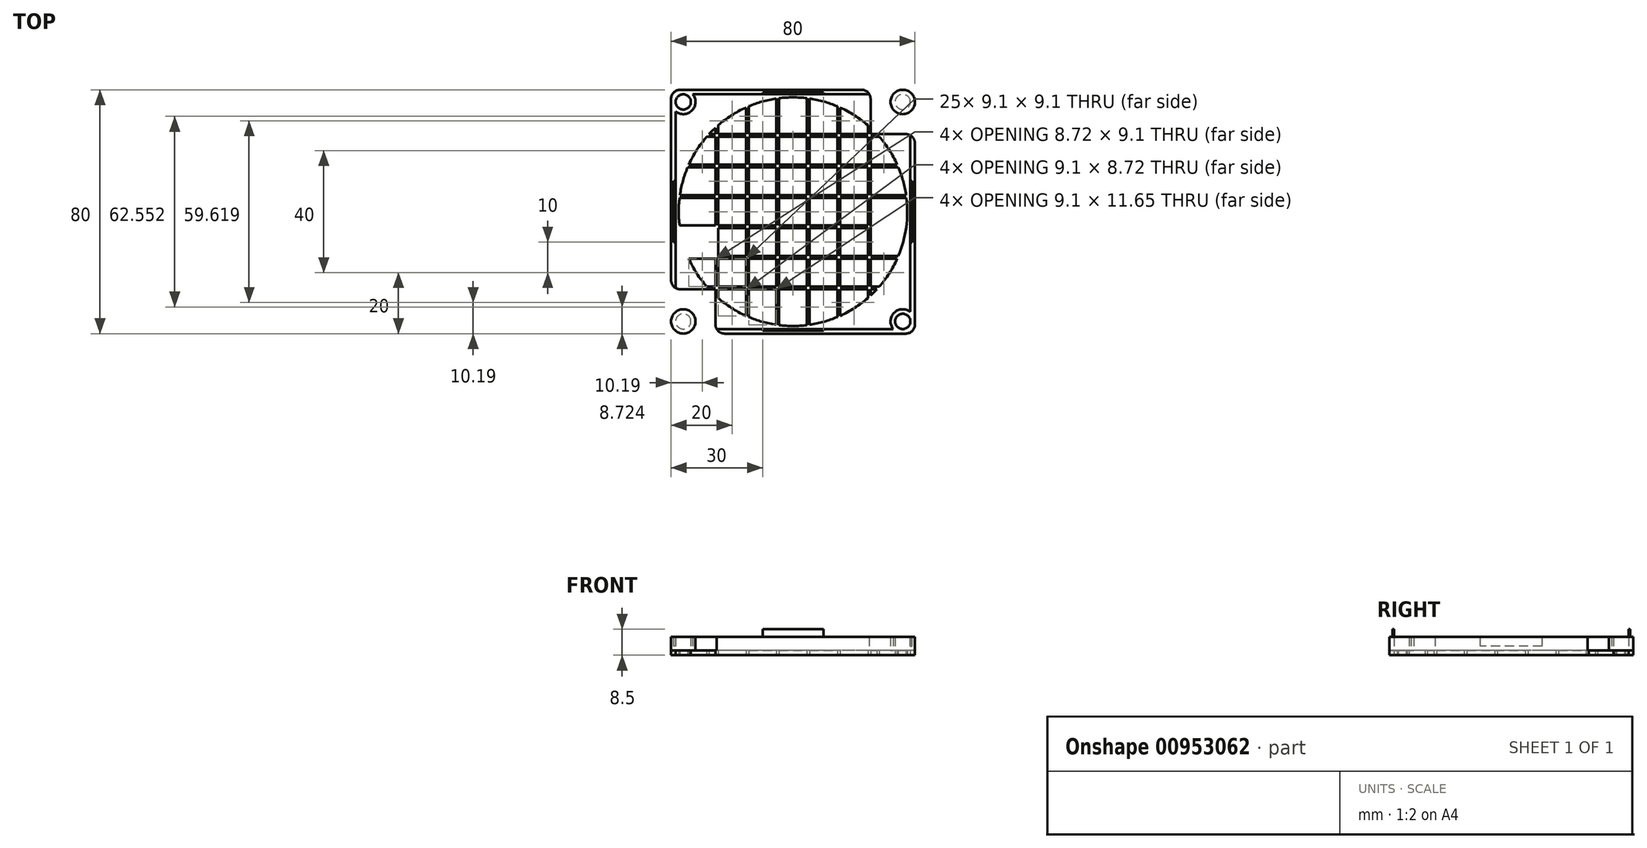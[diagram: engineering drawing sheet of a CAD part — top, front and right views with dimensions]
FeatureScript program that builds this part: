
annotation { "Feature Type Name" : "Feature", "Feature Type Description" : "" }
export const myFeature = defineFeature(function(context is Context, id is Id, definition is map)
    precondition{}
    {
        {
            var Q0;
            Q0=qCreatedBy(makeId("Top.planeOp"),FACE);
            var sketch = newSketch(context, id + "F0", { "sketchPlane" : qUnion([Q0])});
            skLineSegment(sketch, "E0.bottom", {"start": v(40, 40) * mm, "end": v(-40, 40) * mm});
            skLineSegment(sketch, "E0.top", {"start": v(40, -40) * mm, "end": v(-40, -40) * mm});
            skLineSegment(sketch, "E0.left", {"start": v(40, 40) * mm, "end": v(40, -40) * mm});
            skLineSegment(sketch, "E0.right", {"start": v(-40, 40) * mm, "end": v(-40, -40) * mm});
            skPoint(sketch, "E0.middle", {"position": v(0, 0) * mm});
            skCircle(sketch, "E1", {"center": v(-36, 36) * mm, "radius": 2.5 * mm});
            skCircle(sketch, "E2.MirrorC", {"center": v(36, 36) * mm, "radius": 2.5 * mm});
            skCircle(sketch, "E3.MirrorC", {"center": v(-36, -36) * mm, "radius": 2.5 * mm});
            skCircle(sketch, "E4.MirrorC", {"center": v(36, -36) * mm, "radius": 2.5 * mm});
            skCircle(sketch, "E5", {"center": v(0, 0) * mm, "radius": 37.5 * mm});
            skLineSegment(sketch, "E6.bottom", {"start": v(48.46, 5.45) * mm, "end": v(-48.46, 5.45) * mm});
            skLineSegment(sketch, "E6.top", {"start": v(48.46, 4.55) * mm, "end": v(-48.46, 4.55) * mm});
            skLineSegment(sketch, "E6.left", {"start": v(48.46, 5.45) * mm, "end": v(48.46, 4.55) * mm});
            skLineSegment(sketch, "E6.right", {"start": v(-48.46, 5.45) * mm, "end": v(-48.46, 4.55) * mm});
            skPoint(sketch, "E6.middle", {"position": v(0, 5) * mm});
            skLineSegment(sketch, "E7.bottom", {"start": v(55.87, 14.55) * mm, "end": v(-55.87, 14.55) * mm});
            skLineSegment(sketch, "E7.top", {"start": v(55.87, 15.45) * mm, "end": v(-55.87, 15.45) * mm});
            skLineSegment(sketch, "E7.left", {"start": v(55.87, 14.55) * mm, "end": v(55.87, 15.45) * mm});
            skLineSegment(sketch, "E7.right", {"start": v(-55.87, 14.55) * mm, "end": v(-55.87, 15.45) * mm});
            skPoint(sketch, "E7.middle", {"position": v(0, 15) * mm});
            skLineSegment(sketch, "E8.bottom", {"start": v(61.16, 24.55) * mm, "end": v(-61.16, 24.55) * mm});
            skLineSegment(sketch, "E8.top", {"start": v(61.16, 25.45) * mm, "end": v(-61.16, 25.45) * mm});
            skLineSegment(sketch, "E8.left", {"start": v(61.16, 24.55) * mm, "end": v(61.16, 25.45) * mm});
            skLineSegment(sketch, "E8.right", {"start": v(-61.16, 24.55) * mm, "end": v(-61.16, 25.45) * mm});
            skPoint(sketch, "E8.middle", {"position": v(0, 25) * mm});
            skLineSegment(sketch, "E9", {"start": v(0, 0) * mm, "end": v(40, 40) * mm});
            skLineSegment(sketch, "E10.MirrorCS", {"start": v(48.46, -4.55) * mm, "end": v(-48.46, -4.55) * mm});
            skLineSegment(sketch, "E11.MirrorCS", {"start": v(48.46, -5.45) * mm, "end": v(-48.46, -5.45) * mm});
            skLineSegment(sketch, "E12.MirrorCS", {"start": v(55.87, -14.55) * mm, "end": v(-55.87, -14.55) * mm});
            skLineSegment(sketch, "E13.MirrorCS", {"start": v(55.87, -15.45) * mm, "end": v(-55.87, -15.45) * mm});
            skLineSegment(sketch, "E14.MirrorCS", {"start": v(61.16, -24.55) * mm, "end": v(-61.16, -24.55) * mm});
            skLineSegment(sketch, "E15.MirrorCS", {"start": v(61.16, -25.45) * mm, "end": v(-61.16, -25.45) * mm});
            skLineSegment(sketch, "E16.MirrorCS", {"start": v(25.45, 61.16) * mm, "end": v(25.45, -61.16) * mm});
            skLineSegment(sketch, "E17.MirrorCS", {"start": v(24.55, 61.16) * mm, "end": v(24.55, -61.16) * mm});
            skLineSegment(sketch, "E18.MirrorCS", {"start": v(15.45, 55.87) * mm, "end": v(15.45, -55.87) * mm});
            skLineSegment(sketch, "E19.MirrorCS", {"start": v(14.55, 55.87) * mm, "end": v(14.55, -55.87) * mm});
            skLineSegment(sketch, "E20.MirrorCS", {"start": v(5.45, 48.46) * mm, "end": v(5.45, -48.46) * mm});
            skLineSegment(sketch, "E21.MirrorCS", {"start": v(4.55, 48.46) * mm, "end": v(4.55, -48.46) * mm});
            skLineSegment(sketch, "E22.MirrorCS", {"start": v(-4.55, 48.46) * mm, "end": v(-4.55, -48.46) * mm});
            skLineSegment(sketch, "E23.MirrorCS", {"start": v(-5.45, 48.46) * mm, "end": v(-5.45, -48.46) * mm});
            skLineSegment(sketch, "E24.MirrorCS", {"start": v(-14.55, 55.87) * mm, "end": v(-14.55, -55.87) * mm});
            skLineSegment(sketch, "E25.MirrorCS", {"start": v(-15.45, 55.87) * mm, "end": v(-15.45, -55.87) * mm});
            skLineSegment(sketch, "E26.MirrorCS", {"start": v(-24.55, 61.16) * mm, "end": v(-24.55, -61.16) * mm});
            skLineSegment(sketch, "E27.MirrorCS", {"start": v(-25.45, 61.16) * mm, "end": v(-25.45, -61.16) * mm});
            skSolve(sketch);
        }
        {
            var Q0;
            Q0=makeQuery(id+"F0.imprint","IMPRINT",FACE,{"disambiguationData":[TD([[makeQuery(id+"F0.imprint","IMPRINT",EDGE,{"derivedFrom":sQuery(id+"F0.wireOp",EDGE,"E0.bottom")}),1.0]])]});
            var Q1;
            Q1=makeQuery(id+"F0.imprint","IMPRINT",FACE,{"disambiguationData":[TD([[makeQuery(id+"F0.imprint","IMPRINT",EDGE,{"derivedFrom":sQuery(id+"F0.wireOp",EDGE,"E1")}),-1.0]])]});
            var Q2;
            {var subQ0=sQuery(id+"F0.wireOp",EDGE,"E8.bottom");var subQ1=sQuery(id+"F0.wireOp",EDGE,"E0.right");var subQ2=makeQuery(id+"F0.imprint","INTERSECT",VERTEX,{"derivedFrom":[subQ1,subQ0]});Q2=makeQuery(id+"F0.imprint","IMPRINT",FACE,{"disambiguationData":[TD([[makeQuery(id+"F0.imprint","IMPRINT",EDGE,{"disambiguationData":[TD([[subQ2,-1.0]])],"derivedFrom":subQ1}),1.0]])]});}
            var Q3;
            {var subQ0=sQuery(id+"F0.wireOp",EDGE,"E8.top");var subQ1=sQuery(id+"F0.wireOp",EDGE,"E0.right");var subQ2=makeQuery(id+"F0.imprint","INTERSECT",VERTEX,{"derivedFrom":[subQ1,subQ0]});Q3=makeQuery(id+"F0.imprint","IMPRINT",FACE,{"disambiguationData":[TD([[makeQuery(id+"F0.imprint","IMPRINT",EDGE,{"disambiguationData":[TD([[subQ2,-1.0]])],"derivedFrom":subQ1}),1.0]])]});}
            var Q4;
            {var subQ0=sQuery(id+"F0.wireOp",EDGE,"E26.MirrorCS");var subQ1=sQuery(id+"F0.wireOp",EDGE,"E8.bottom");var subQ2=makeQuery(id+"F0.imprint","INTERSECT",VERTEX,{"derivedFrom":[subQ1,subQ0]});Q4=makeQuery(id+"F0.imprint","IMPRINT",FACE,{"disambiguationData":[TD([[makeQuery(id+"F0.imprint","IMPRINT",EDGE,{"disambiguationData":[TD([[subQ2,-1.0]])],"derivedFrom":subQ1}),-1.0]])]});}
            var Q5;
            {var subQ0=sQuery(id+"F0.wireOp",EDGE,"E26.MirrorCS");var subQ1=sQuery(id+"F0.wireOp",EDGE,"E5");var subQ2=makeQuery(id+"F0.imprint","INTERSECT",VERTEX,{"disambiguationData":[OD(0.0)],"derivedFrom":[subQ1,subQ0]});Q5=makeQuery(id+"F0.imprint","IMPRINT",FACE,{"disambiguationData":[TD([[makeQuery(id+"F0.imprint","IMPRINT",EDGE,{"disambiguationData":[TD([[subQ2,-1.0]])],"derivedFrom":subQ1}),1.0]])]});}
            var Q6;
            {var subQ0=sQuery(id+"F0.wireOp",EDGE,"E8.top");var subQ1=sQuery(id+"F0.wireOp",EDGE,"E5");var subQ2=makeQuery(id+"F0.imprint","INTERSECT",VERTEX,{"disambiguationData":[OD(1.0)],"derivedFrom":[subQ1,subQ0]});Q6=makeQuery(id+"F0.imprint","IMPRINT",FACE,{"disambiguationData":[TD([[makeQuery(id+"F0.imprint","IMPRINT",EDGE,{"disambiguationData":[TD([[subQ2,-1.0]])],"derivedFrom":subQ1}),1.0]])]});}
            var Q7;
            {var subQ0=sQuery(id+"F0.wireOp",EDGE,"E9");var subQ5=sQuery(id+"F0.wireOp",EDGE,"E2.MirrorC");var subQ6=makeQuery(id+"F0.imprint","INTERSECT",VERTEX,{"disambiguationData":[OD(0.0)],"derivedFrom":[subQ5,subQ0]});Q7=makeQuery(id+"F0.imprint","IMPRINT",FACE,{"disambiguationData":[TD([[makeQuery(id+"F0.imprint","IMPRINT",EDGE,{"disambiguationData":[TD([[subQ6,-1.0]])],"derivedFrom":subQ5}),1.0]])]});}
            var Q8;
            {var subQ0=sQuery(id+"F0.wireOp",EDGE,"E13.MirrorCS");var subQ1=sQuery(id+"F0.wireOp",EDGE,"E0.left");var subQ2=makeQuery(id+"F0.imprint","INTERSECT",VERTEX,{"derivedFrom":[subQ1,subQ0]});Q8=makeQuery(id+"F0.imprint","IMPRINT",FACE,{"disambiguationData":[TD([[makeQuery(id+"F0.imprint","IMPRINT",EDGE,{"disambiguationData":[TD([[subQ2,-1.0]])],"derivedFrom":subQ1}),-1.0]])]});}
            var Q9;
            {var subQ0=sQuery(id+"F0.wireOp",EDGE,"E11.MirrorCS");var subQ1=sQuery(id+"F0.wireOp",EDGE,"E0.left");var subQ2=makeQuery(id+"F0.imprint","INTERSECT",VERTEX,{"derivedFrom":[subQ1,subQ0]});Q9=makeQuery(id+"F0.imprint","IMPRINT",FACE,{"disambiguationData":[TD([[makeQuery(id+"F0.imprint","IMPRINT",EDGE,{"disambiguationData":[TD([[subQ2,-1.0]])],"derivedFrom":subQ1}),-1.0]])]});}
            var Q10;
            {var subQ0=sQuery(id+"F0.wireOp",EDGE,"E7.bottom");var subQ1=sQuery(id+"F0.wireOp",EDGE,"E0.left");var subQ2=makeQuery(id+"F0.imprint","INTERSECT",VERTEX,{"derivedFrom":[subQ1,subQ0]});Q10=makeQuery(id+"F0.imprint","IMPRINT",FACE,{"disambiguationData":[TD([[makeQuery(id+"F0.imprint","IMPRINT",EDGE,{"disambiguationData":[TD([[subQ2,-1.0]])],"derivedFrom":subQ1}),-1.0]])]});}
            var Q11;
            {var subQ0=sQuery(id+"F0.wireOp",EDGE,"E8.bottom");var subQ1=sQuery(id+"F0.wireOp",EDGE,"E0.left");var subQ2=makeQuery(id+"F0.imprint","INTERSECT",VERTEX,{"derivedFrom":[subQ1,subQ0]});Q11=makeQuery(id+"F0.imprint","IMPRINT",FACE,{"disambiguationData":[TD([[makeQuery(id+"F0.imprint","IMPRINT",EDGE,{"disambiguationData":[TD([[subQ2,-1.0]])],"derivedFrom":subQ1}),-1.0]])]});}
            var Q12;
            {var subQ0=sQuery(id+"F0.wireOp",EDGE,"E8.top");var subQ1=sQuery(id+"F0.wireOp",EDGE,"E0.left");var subQ2=makeQuery(id+"F0.imprint","INTERSECT",VERTEX,{"derivedFrom":[subQ1,subQ0]});Q12=makeQuery(id+"F0.imprint","IMPRINT",FACE,{"disambiguationData":[TD([[makeQuery(id+"F0.imprint","IMPRINT",EDGE,{"disambiguationData":[TD([[subQ2,-1.0]])],"derivedFrom":subQ1}),-1.0]])]});}
            var Q13;
            {var subQ0=sQuery(id+"F0.wireOp",EDGE,"E25.MirrorCS");var subQ1=sQuery(id+"F0.wireOp",EDGE,"E0.top");var subQ2=makeQuery(id+"F0.imprint","INTERSECT",VERTEX,{"derivedFrom":[subQ1,subQ0]});Q13=makeQuery(id+"F0.imprint","IMPRINT",FACE,{"disambiguationData":[TD([[makeQuery(id+"F0.imprint","IMPRINT",EDGE,{"disambiguationData":[TD([[subQ2,-1.0]])],"derivedFrom":subQ1}),-1.0]])]});}
            var Q14;
            {var subQ0=sQuery(id+"F0.wireOp",EDGE,"E23.MirrorCS");var subQ1=sQuery(id+"F0.wireOp",EDGE,"E0.top");var subQ2=makeQuery(id+"F0.imprint","INTERSECT",VERTEX,{"derivedFrom":[subQ1,subQ0]});Q14=makeQuery(id+"F0.imprint","IMPRINT",FACE,{"disambiguationData":[TD([[makeQuery(id+"F0.imprint","IMPRINT",EDGE,{"disambiguationData":[TD([[subQ2,-1.0]])],"derivedFrom":subQ1}),-1.0]])]});}
            var Q15;
            {var subQ0=sQuery(id+"F0.wireOp",EDGE,"E11.MirrorCS");var subQ1=sQuery(id+"F0.wireOp",EDGE,"E0.right");var subQ2=makeQuery(id+"F0.imprint","INTERSECT",VERTEX,{"derivedFrom":[subQ1,subQ0]});Q15=makeQuery(id+"F0.imprint","IMPRINT",FACE,{"disambiguationData":[TD([[makeQuery(id+"F0.imprint","IMPRINT",EDGE,{"disambiguationData":[TD([[subQ2,-1.0]])],"derivedFrom":subQ1}),1.0]])]});}
            var Q16;
            {var subQ0=sQuery(id+"F0.wireOp",EDGE,"E7.bottom");var subQ1=sQuery(id+"F0.wireOp",EDGE,"E0.right");var subQ2=makeQuery(id+"F0.imprint","INTERSECT",VERTEX,{"derivedFrom":[subQ1,subQ0]});Q16=makeQuery(id+"F0.imprint","IMPRINT",FACE,{"disambiguationData":[TD([[makeQuery(id+"F0.imprint","IMPRINT",EDGE,{"disambiguationData":[TD([[subQ2,-1.0]])],"derivedFrom":subQ1}),1.0]])]});}
            var Q17;
            {var subQ0=sQuery(id+"F0.wireOp",EDGE,"E6.bottom");var subQ1=sQuery(id+"F0.wireOp",EDGE,"E5");var subQ2=makeQuery(id+"F0.imprint","INTERSECT",VERTEX,{"disambiguationData":[OD(1.0)],"derivedFrom":[subQ1,subQ0]});Q17=makeQuery(id+"F0.imprint","IMPRINT",FACE,{"disambiguationData":[TD([[makeQuery(id+"F0.imprint","IMPRINT",EDGE,{"disambiguationData":[TD([[subQ2,-1.0]])],"derivedFrom":subQ1}),1.0]])]});}
            var Q18;
            {var subQ0=sQuery(id+"F0.wireOp",EDGE,"E12.MirrorCS");var subQ1=sQuery(id+"F0.wireOp",EDGE,"E5");var subQ2=makeQuery(id+"F0.imprint","INTERSECT",VERTEX,{"disambiguationData":[OD(0.0)],"derivedFrom":[subQ1,subQ0]});Q18=makeQuery(id+"F0.imprint","IMPRINT",FACE,{"disambiguationData":[TD([[makeQuery(id+"F0.imprint","IMPRINT",EDGE,{"disambiguationData":[TD([[subQ2,-1.0]])],"derivedFrom":subQ1}),1.0]])]});}
            var Q19;
            {var subQ0=sQuery(id+"F0.wireOp",EDGE,"E10.MirrorCS");var subQ1=sQuery(id+"F0.wireOp",EDGE,"E5");var subQ2=makeQuery(id+"F0.imprint","INTERSECT",VERTEX,{"disambiguationData":[OD(0.0)],"derivedFrom":[subQ1,subQ0]});Q19=makeQuery(id+"F0.imprint","IMPRINT",FACE,{"disambiguationData":[TD([[makeQuery(id+"F0.imprint","IMPRINT",EDGE,{"disambiguationData":[TD([[subQ2,-1.0]])],"derivedFrom":subQ1}),1.0]])]});}
            var Q20;
            {var subQ0=sQuery(id+"F0.wireOp",EDGE,"E26.MirrorCS");var subQ1=sQuery(id+"F0.wireOp",EDGE,"E10.MirrorCS");var subQ2=makeQuery(id+"F0.imprint","INTERSECT",VERTEX,{"derivedFrom":[subQ1,subQ0]});Q20=makeQuery(id+"F0.imprint","IMPRINT",FACE,{"disambiguationData":[TD([[makeQuery(id+"F0.imprint","IMPRINT",EDGE,{"disambiguationData":[TD([[subQ2,-1.0]])],"derivedFrom":subQ1}),1.0]])]});}
            var Q21;
            {var subQ0=sQuery(id+"F0.wireOp",EDGE,"E26.MirrorCS");var subQ1=sQuery(id+"F0.wireOp",EDGE,"E6.top");var subQ2=makeQuery(id+"F0.imprint","INTERSECT",VERTEX,{"derivedFrom":[subQ1,subQ0]});Q21=makeQuery(id+"F0.imprint","IMPRINT",FACE,{"disambiguationData":[TD([[makeQuery(id+"F0.imprint","IMPRINT",EDGE,{"disambiguationData":[TD([[subQ2,-1.0]])],"derivedFrom":subQ1}),1.0]])]});}
            var Q22;
            {var subQ0=sQuery(id+"F0.wireOp",EDGE,"E26.MirrorCS");var subQ1=sQuery(id+"F0.wireOp",EDGE,"E6.bottom");var subQ2=makeQuery(id+"F0.imprint","INTERSECT",VERTEX,{"derivedFrom":[subQ1,subQ0]});Q22=makeQuery(id+"F0.imprint","IMPRINT",FACE,{"disambiguationData":[TD([[makeQuery(id+"F0.imprint","IMPRINT",EDGE,{"disambiguationData":[TD([[subQ2,-1.0]])],"derivedFrom":subQ1}),1.0]])]});}
            var Q23;
            {var subQ0=sQuery(id+"F0.wireOp",EDGE,"E26.MirrorCS");var subQ1=sQuery(id+"F0.wireOp",EDGE,"E6.bottom");var subQ2=makeQuery(id+"F0.imprint","INTERSECT",VERTEX,{"derivedFrom":[subQ1,subQ0]});Q23=makeQuery(id+"F0.imprint","IMPRINT",FACE,{"disambiguationData":[TD([[makeQuery(id+"F0.imprint","IMPRINT",EDGE,{"disambiguationData":[TD([[subQ2,-1.0]])],"derivedFrom":subQ1}),-1.0]])]});}
            var Q24;
            {var subQ0=sQuery(id+"F0.wireOp",EDGE,"E26.MirrorCS");var subQ1=sQuery(id+"F0.wireOp",EDGE,"E7.bottom");var subQ2=makeQuery(id+"F0.imprint","INTERSECT",VERTEX,{"derivedFrom":[subQ1,subQ0]});Q24=makeQuery(id+"F0.imprint","IMPRINT",FACE,{"disambiguationData":[TD([[makeQuery(id+"F0.imprint","IMPRINT",EDGE,{"disambiguationData":[TD([[subQ2,-1.0]])],"derivedFrom":subQ1}),-1.0]])]});}
            var Q25;
            {var subQ0=sQuery(id+"F0.wireOp",EDGE,"E7.top");var subQ1=sQuery(id+"F0.wireOp",EDGE,"E5");var subQ2=makeQuery(id+"F0.imprint","INTERSECT",VERTEX,{"disambiguationData":[OD(1.0)],"derivedFrom":[subQ1,subQ0]});Q25=makeQuery(id+"F0.imprint","IMPRINT",FACE,{"disambiguationData":[TD([[makeQuery(id+"F0.imprint","IMPRINT",EDGE,{"disambiguationData":[TD([[subQ2,-1.0]])],"derivedFrom":subQ1}),1.0]])]});}
            var Q26;
            {var subQ0=sQuery(id+"F0.wireOp",EDGE,"E26.MirrorCS");var subQ1=sQuery(id+"F0.wireOp",EDGE,"E7.top");var subQ2=makeQuery(id+"F0.imprint","INTERSECT",VERTEX,{"derivedFrom":[subQ1,subQ0]});Q26=makeQuery(id+"F0.imprint","IMPRINT",FACE,{"disambiguationData":[TD([[makeQuery(id+"F0.imprint","IMPRINT",EDGE,{"disambiguationData":[TD([[subQ2,-1.0]])],"derivedFrom":subQ1}),-1.0]])]});}
            var Q27;
            {var subQ0=sQuery(id+"F0.wireOp",EDGE,"E7.top");var subQ1=sQuery(id+"F0.wireOp",EDGE,"E0.right");var subQ2=makeQuery(id+"F0.imprint","INTERSECT",VERTEX,{"derivedFrom":[subQ1,subQ0]});Q27=makeQuery(id+"F0.imprint","IMPRINT",FACE,{"disambiguationData":[TD([[makeQuery(id+"F0.imprint","IMPRINT",EDGE,{"disambiguationData":[TD([[subQ2,-1.0]])],"derivedFrom":subQ1}),1.0]])]});}
            var Q28;
            {var subQ0=sQuery(id+"F0.wireOp",EDGE,"E6.bottom");var subQ1=sQuery(id+"F0.wireOp",EDGE,"E0.right");var subQ2=makeQuery(id+"F0.imprint","INTERSECT",VERTEX,{"derivedFrom":[subQ1,subQ0]});Q28=makeQuery(id+"F0.imprint","IMPRINT",FACE,{"disambiguationData":[TD([[makeQuery(id+"F0.imprint","IMPRINT",EDGE,{"disambiguationData":[TD([[subQ2,-1.0]])],"derivedFrom":subQ1}),1.0]])]});}
            var Q29;
            {var subQ0=sQuery(id+"F0.wireOp",EDGE,"E10.MirrorCS");var subQ1=sQuery(id+"F0.wireOp",EDGE,"E0.right");var subQ2=makeQuery(id+"F0.imprint","INTERSECT",VERTEX,{"derivedFrom":[subQ1,subQ0]});Q29=makeQuery(id+"F0.imprint","IMPRINT",FACE,{"disambiguationData":[TD([[makeQuery(id+"F0.imprint","IMPRINT",EDGE,{"disambiguationData":[TD([[subQ2,1.0]])],"derivedFrom":subQ1}),1.0]])]});}
            var Q30;
            {var subQ0=sQuery(id+"F0.wireOp",EDGE,"E10.MirrorCS");var subQ1=sQuery(id+"F0.wireOp",EDGE,"E0.right");var subQ2=makeQuery(id+"F0.imprint","INTERSECT",VERTEX,{"derivedFrom":[subQ1,subQ0]});Q30=makeQuery(id+"F0.imprint","IMPRINT",FACE,{"disambiguationData":[TD([[makeQuery(id+"F0.imprint","IMPRINT",EDGE,{"disambiguationData":[TD([[subQ2,-1.0]])],"derivedFrom":subQ1}),1.0]])]});}
            var Q31;
            {var subQ0=sQuery(id+"F0.wireOp",EDGE,"E12.MirrorCS");var subQ1=sQuery(id+"F0.wireOp",EDGE,"E0.right");var subQ2=makeQuery(id+"F0.imprint","INTERSECT",VERTEX,{"derivedFrom":[subQ1,subQ0]});Q31=makeQuery(id+"F0.imprint","IMPRINT",FACE,{"disambiguationData":[TD([[makeQuery(id+"F0.imprint","IMPRINT",EDGE,{"disambiguationData":[TD([[subQ2,-1.0]])],"derivedFrom":subQ1}),1.0]])]});}
            var Q32;
            {var subQ0=sQuery(id+"F0.wireOp",EDGE,"E13.MirrorCS");var subQ1=sQuery(id+"F0.wireOp",EDGE,"E0.right");var subQ2=makeQuery(id+"F0.imprint","INTERSECT",VERTEX,{"derivedFrom":[subQ1,subQ0]});Q32=makeQuery(id+"F0.imprint","IMPRINT",FACE,{"disambiguationData":[TD([[makeQuery(id+"F0.imprint","IMPRINT",EDGE,{"disambiguationData":[TD([[subQ2,-1.0]])],"derivedFrom":subQ1}),1.0]])]});}
            var Q33;
            {var subQ0=sQuery(id+"F0.wireOp",EDGE,"E14.MirrorCS");var subQ1=sQuery(id+"F0.wireOp",EDGE,"E0.right");var subQ2=makeQuery(id+"F0.imprint","INTERSECT",VERTEX,{"derivedFrom":[subQ1,subQ0]});Q33=makeQuery(id+"F0.imprint","IMPRINT",FACE,{"disambiguationData":[TD([[makeQuery(id+"F0.imprint","IMPRINT",EDGE,{"disambiguationData":[TD([[subQ2,-1.0]])],"derivedFrom":subQ1}),1.0]])]});}
            var Q34;
            Q34=makeQuery(id+"F0.imprint","IMPRINT",FACE,{"disambiguationData":[TD([[makeQuery(id+"F0.imprint","IMPRINT",EDGE,{"derivedFrom":sQuery(id+"F0.wireOp",EDGE,"E3.MirrorC")}),1.0]])]});
            var Q35;
            {var subQ0=sQuery(id+"F0.wireOp",EDGE,"E26.MirrorCS");var subQ1=sQuery(id+"F0.wireOp",EDGE,"E0.top");var subQ2=makeQuery(id+"F0.imprint","INTERSECT",VERTEX,{"derivedFrom":[subQ1,subQ0]});Q35=makeQuery(id+"F0.imprint","IMPRINT",FACE,{"disambiguationData":[TD([[makeQuery(id+"F0.imprint","IMPRINT",EDGE,{"disambiguationData":[TD([[subQ2,-1.0]])],"derivedFrom":subQ1}),-1.0]])]});}
            var Q36;
            {var subQ0=sQuery(id+"F0.wireOp",EDGE,"E24.MirrorCS");var subQ1=sQuery(id+"F0.wireOp",EDGE,"E0.top");var subQ2=makeQuery(id+"F0.imprint","INTERSECT",VERTEX,{"derivedFrom":[subQ1,subQ0]});Q36=makeQuery(id+"F0.imprint","IMPRINT",FACE,{"disambiguationData":[TD([[makeQuery(id+"F0.imprint","IMPRINT",EDGE,{"disambiguationData":[TD([[subQ2,-1.0]])],"derivedFrom":subQ1}),-1.0]])]});}
            var Q37;
            {var subQ0=sQuery(id+"F0.wireOp",EDGE,"E25.MirrorCS");var subQ1=sQuery(id+"F0.wireOp",EDGE,"E5");var subQ2=makeQuery(id+"F0.imprint","INTERSECT",VERTEX,{"disambiguationData":[OD(1.0)],"derivedFrom":[subQ1,subQ0]});Q37=makeQuery(id+"F0.imprint","IMPRINT",FACE,{"disambiguationData":[TD([[makeQuery(id+"F0.imprint","IMPRINT",EDGE,{"disambiguationData":[TD([[subQ2,-1.0]])],"derivedFrom":subQ1}),1.0]])]});}
            var Q38;
            {var subQ0=sQuery(id+"F0.wireOp",EDGE,"E24.MirrorCS");var subQ1=sQuery(id+"F0.wireOp",EDGE,"E14.MirrorCS");var subQ2=makeQuery(id+"F0.imprint","INTERSECT",VERTEX,{"derivedFrom":[subQ1,subQ0]});Q38=makeQuery(id+"F0.imprint","IMPRINT",FACE,{"disambiguationData":[TD([[makeQuery(id+"F0.imprint","IMPRINT",EDGE,{"disambiguationData":[TD([[subQ2,-1.0]])],"derivedFrom":subQ1}),1.0]])]});}
            var Q39;
            {var subQ0=sQuery(id+"F0.wireOp",EDGE,"E25.MirrorCS");var subQ1=sQuery(id+"F0.wireOp",EDGE,"E14.MirrorCS");var subQ2=makeQuery(id+"F0.imprint","INTERSECT",VERTEX,{"derivedFrom":[subQ1,subQ0]});Q39=makeQuery(id+"F0.imprint","IMPRINT",FACE,{"disambiguationData":[TD([[makeQuery(id+"F0.imprint","IMPRINT",EDGE,{"disambiguationData":[TD([[subQ2,-1.0]])],"derivedFrom":subQ1}),1.0]])]});}
            var Q40;
            {var subQ0=sQuery(id+"F0.wireOp",EDGE,"E24.MirrorCS");var subQ1=sQuery(id+"F0.wireOp",EDGE,"E13.MirrorCS");var subQ2=makeQuery(id+"F0.imprint","INTERSECT",VERTEX,{"derivedFrom":[subQ1,subQ0]});Q40=makeQuery(id+"F0.imprint","IMPRINT",FACE,{"disambiguationData":[TD([[makeQuery(id+"F0.imprint","IMPRINT",EDGE,{"disambiguationData":[TD([[subQ2,-1.0]])],"derivedFrom":subQ1}),1.0]])]});}
            var Q41;
            {var subQ0=sQuery(id+"F0.wireOp",EDGE,"E23.MirrorCS");var subQ1=sQuery(id+"F0.wireOp",EDGE,"E14.MirrorCS");var subQ2=makeQuery(id+"F0.imprint","INTERSECT",VERTEX,{"derivedFrom":[subQ1,subQ0]});Q41=makeQuery(id+"F0.imprint","IMPRINT",FACE,{"disambiguationData":[TD([[makeQuery(id+"F0.imprint","IMPRINT",EDGE,{"disambiguationData":[TD([[subQ2,-1.0]])],"derivedFrom":subQ1}),1.0]])]});}
            var Q42;
            {var subQ0=sQuery(id+"F0.wireOp",EDGE,"E22.MirrorCS");var subQ1=sQuery(id+"F0.wireOp",EDGE,"E13.MirrorCS");var subQ2=makeQuery(id+"F0.imprint","INTERSECT",VERTEX,{"derivedFrom":[subQ1,subQ0]});Q42=makeQuery(id+"F0.imprint","IMPRINT",FACE,{"disambiguationData":[TD([[makeQuery(id+"F0.imprint","IMPRINT",EDGE,{"disambiguationData":[TD([[subQ2,-1.0]])],"derivedFrom":subQ1}),1.0]])]});}
            var Q43;
            {var subQ0=sQuery(id+"F0.wireOp",EDGE,"E22.MirrorCS");var subQ1=sQuery(id+"F0.wireOp",EDGE,"E12.MirrorCS");var subQ2=makeQuery(id+"F0.imprint","INTERSECT",VERTEX,{"derivedFrom":[subQ1,subQ0]});Q43=makeQuery(id+"F0.imprint","IMPRINT",FACE,{"disambiguationData":[TD([[makeQuery(id+"F0.imprint","IMPRINT",EDGE,{"disambiguationData":[TD([[subQ2,-1.0]])],"derivedFrom":subQ1}),1.0]])]});}
            var Q44;
            {var subQ0=sQuery(id+"F0.wireOp",EDGE,"E22.MirrorCS");var subQ1=sQuery(id+"F0.wireOp",EDGE,"E11.MirrorCS");var subQ2=makeQuery(id+"F0.imprint","INTERSECT",VERTEX,{"derivedFrom":[subQ1,subQ0]});Q44=makeQuery(id+"F0.imprint","IMPRINT",FACE,{"disambiguationData":[TD([[makeQuery(id+"F0.imprint","IMPRINT",EDGE,{"disambiguationData":[TD([[subQ2,-1.0]])],"derivedFrom":subQ1}),1.0]])]});}
            var Q45;
            {var subQ0=sQuery(id+"F0.wireOp",EDGE,"E21.MirrorCS");var subQ1=sQuery(id+"F0.wireOp",EDGE,"E12.MirrorCS");var subQ2=makeQuery(id+"F0.imprint","INTERSECT",VERTEX,{"derivedFrom":[subQ1,subQ0]});Q45=makeQuery(id+"F0.imprint","IMPRINT",FACE,{"disambiguationData":[TD([[makeQuery(id+"F0.imprint","IMPRINT",EDGE,{"disambiguationData":[TD([[subQ2,-1.0]])],"derivedFrom":subQ1}),1.0]])]});}
            var Q46;
            {var subQ0=sQuery(id+"F0.wireOp",EDGE,"E20.MirrorCS");var subQ1=sQuery(id+"F0.wireOp",EDGE,"E12.MirrorCS");var subQ2=makeQuery(id+"F0.imprint","INTERSECT",VERTEX,{"derivedFrom":[subQ1,subQ0]});Q46=makeQuery(id+"F0.imprint","IMPRINT",FACE,{"disambiguationData":[TD([[makeQuery(id+"F0.imprint","IMPRINT",EDGE,{"disambiguationData":[TD([[subQ2,-1.0]])],"derivedFrom":subQ1}),1.0]])]});}
            var Q47;
            {var subQ0=sQuery(id+"F0.wireOp",EDGE,"E20.MirrorCS");var subQ1=sQuery(id+"F0.wireOp",EDGE,"E13.MirrorCS");var subQ2=makeQuery(id+"F0.imprint","INTERSECT",VERTEX,{"derivedFrom":[subQ1,subQ0]});Q47=makeQuery(id+"F0.imprint","IMPRINT",FACE,{"disambiguationData":[TD([[makeQuery(id+"F0.imprint","IMPRINT",EDGE,{"disambiguationData":[TD([[subQ2,-1.0]])],"derivedFrom":subQ1}),1.0]])]});}
            var Q48;
            {var subQ0=sQuery(id+"F0.wireOp",EDGE,"E20.MirrorCS");var subQ1=sQuery(id+"F0.wireOp",EDGE,"E11.MirrorCS");var subQ2=makeQuery(id+"F0.imprint","INTERSECT",VERTEX,{"derivedFrom":[subQ1,subQ0]});Q48=makeQuery(id+"F0.imprint","IMPRINT",FACE,{"disambiguationData":[TD([[makeQuery(id+"F0.imprint","IMPRINT",EDGE,{"disambiguationData":[TD([[subQ2,-1.0]])],"derivedFrom":subQ1}),1.0]])]});}
            var Q49;
            {var subQ0=sQuery(id+"F0.wireOp",EDGE,"E19.MirrorCS");var subQ1=sQuery(id+"F0.wireOp",EDGE,"E12.MirrorCS");var subQ2=makeQuery(id+"F0.imprint","INTERSECT",VERTEX,{"derivedFrom":[subQ1,subQ0]});Q49=makeQuery(id+"F0.imprint","IMPRINT",FACE,{"disambiguationData":[TD([[makeQuery(id+"F0.imprint","IMPRINT",EDGE,{"disambiguationData":[TD([[subQ2,-1.0]])],"derivedFrom":subQ1}),1.0]])]});}
            var Q50;
            {var subQ0=sQuery(id+"F0.wireOp",EDGE,"E17.MirrorCS");var subQ1=sQuery(id+"F0.wireOp",EDGE,"E14.MirrorCS");var subQ2=makeQuery(id+"F0.imprint","INTERSECT",VERTEX,{"derivedFrom":[subQ1,subQ0]});Q50=makeQuery(id+"F0.imprint","IMPRINT",FACE,{"disambiguationData":[TD([[makeQuery(id+"F0.imprint","IMPRINT",EDGE,{"disambiguationData":[TD([[subQ2,-1.0]])],"derivedFrom":subQ1}),1.0]])]});}
            var Q51;
            {var subQ0=sQuery(id+"F0.wireOp",EDGE,"E18.MirrorCS");var subQ1=sQuery(id+"F0.wireOp",EDGE,"E14.MirrorCS");var subQ2=makeQuery(id+"F0.imprint","INTERSECT",VERTEX,{"derivedFrom":[subQ1,subQ0]});Q51=makeQuery(id+"F0.imprint","IMPRINT",FACE,{"disambiguationData":[TD([[makeQuery(id+"F0.imprint","IMPRINT",EDGE,{"disambiguationData":[TD([[subQ2,-1.0]])],"derivedFrom":subQ1}),1.0]])]});}
            var Q52;
            {var subQ0=sQuery(id+"F0.wireOp",EDGE,"E19.MirrorCS");var subQ1=sQuery(id+"F0.wireOp",EDGE,"E14.MirrorCS");var subQ2=makeQuery(id+"F0.imprint","INTERSECT",VERTEX,{"derivedFrom":[subQ1,subQ0]});Q52=makeQuery(id+"F0.imprint","IMPRINT",FACE,{"disambiguationData":[TD([[makeQuery(id+"F0.imprint","IMPRINT",EDGE,{"disambiguationData":[TD([[subQ2,-1.0]])],"derivedFrom":subQ1}),1.0]])]});}
            var Q53;
            {var subQ0=sQuery(id+"F0.wireOp",EDGE,"E19.MirrorCS");var subQ1=sQuery(id+"F0.wireOp",EDGE,"E5");var subQ2=makeQuery(id+"F0.imprint","INTERSECT",VERTEX,{"disambiguationData":[OD(1.0)],"derivedFrom":[subQ1,subQ0]});Q53=makeQuery(id+"F0.imprint","IMPRINT",FACE,{"disambiguationData":[TD([[makeQuery(id+"F0.imprint","IMPRINT",EDGE,{"disambiguationData":[TD([[subQ2,-1.0]])],"derivedFrom":subQ1}),1.0]])]});}
            var Q54;
            {var subQ0=sQuery(id+"F0.wireOp",EDGE,"E17.MirrorCS");var subQ1=sQuery(id+"F0.wireOp",EDGE,"E0.top");var subQ2=makeQuery(id+"F0.imprint","INTERSECT",VERTEX,{"derivedFrom":[subQ1,subQ0]});Q54=makeQuery(id+"F0.imprint","IMPRINT",FACE,{"disambiguationData":[TD([[makeQuery(id+"F0.imprint","IMPRINT",EDGE,{"disambiguationData":[TD([[subQ2,-1.0]])],"derivedFrom":subQ1}),-1.0]])]});}
            var Q55;
            {var subQ0=sQuery(id+"F0.wireOp",EDGE,"E18.MirrorCS");var subQ1=sQuery(id+"F0.wireOp",EDGE,"E0.top");var subQ2=makeQuery(id+"F0.imprint","INTERSECT",VERTEX,{"derivedFrom":[subQ1,subQ0]});Q55=makeQuery(id+"F0.imprint","IMPRINT",FACE,{"disambiguationData":[TD([[makeQuery(id+"F0.imprint","IMPRINT",EDGE,{"disambiguationData":[TD([[subQ2,-1.0]])],"derivedFrom":subQ1}),-1.0]])]});}
            var Q56;
            {var subQ3=sQuery(id+"F0.wireOp",EDGE,"E9");var subQ5=sQuery(id+"F0.wireOp",EDGE,"E2.MirrorC");var subQ6=makeQuery(id+"F0.imprint","INTERSECT",VERTEX,{"disambiguationData":[OD(0.0)],"derivedFrom":[subQ5,subQ3]});Q56=makeQuery(id+"F0.imprint","IMPRINT",FACE,{"disambiguationData":[TD([[makeQuery(id+"F0.imprint","IMPRINT",EDGE,{"disambiguationData":[TD([[subQ6,1.0]])],"derivedFrom":subQ5}),1.0]])]});}
            var Q57;
            {var subQ0=sQuery(id+"F0.wireOp",EDGE,"E7.top");var subQ1=sQuery(id+"F0.wireOp",EDGE,"E0.left");var subQ2=makeQuery(id+"F0.imprint","INTERSECT",VERTEX,{"derivedFrom":[subQ1,subQ0]});Q57=makeQuery(id+"F0.imprint","IMPRINT",FACE,{"disambiguationData":[TD([[makeQuery(id+"F0.imprint","IMPRINT",EDGE,{"disambiguationData":[TD([[subQ2,-1.0]])],"derivedFrom":subQ1}),-1.0]])]});}
            var Q58;
            {var subQ0=sQuery(id+"F0.wireOp",EDGE,"E6.bottom");var subQ1=sQuery(id+"F0.wireOp",EDGE,"E0.left");var subQ2=makeQuery(id+"F0.imprint","INTERSECT",VERTEX,{"derivedFrom":[subQ1,subQ0]});Q58=makeQuery(id+"F0.imprint","IMPRINT",FACE,{"disambiguationData":[TD([[makeQuery(id+"F0.imprint","IMPRINT",EDGE,{"disambiguationData":[TD([[subQ2,-1.0]])],"derivedFrom":subQ1}),-1.0]])]});}
            var Q59;
            {var subQ0=sQuery(id+"F0.wireOp",EDGE,"E10.MirrorCS");var subQ1=sQuery(id+"F0.wireOp",EDGE,"E0.left");var subQ2=makeQuery(id+"F0.imprint","INTERSECT",VERTEX,{"derivedFrom":[subQ1,subQ0]});Q59=makeQuery(id+"F0.imprint","IMPRINT",FACE,{"disambiguationData":[TD([[makeQuery(id+"F0.imprint","IMPRINT",EDGE,{"disambiguationData":[TD([[subQ2,1.0]])],"derivedFrom":subQ1}),-1.0]])]});}
            var Q60;
            {var subQ0=sQuery(id+"F0.wireOp",EDGE,"E10.MirrorCS");var subQ1=sQuery(id+"F0.wireOp",EDGE,"E0.left");var subQ2=makeQuery(id+"F0.imprint","INTERSECT",VERTEX,{"derivedFrom":[subQ1,subQ0]});Q60=makeQuery(id+"F0.imprint","IMPRINT",FACE,{"disambiguationData":[TD([[makeQuery(id+"F0.imprint","IMPRINT",EDGE,{"disambiguationData":[TD([[subQ2,-1.0]])],"derivedFrom":subQ1}),-1.0]])]});}
            var Q61;
            {var subQ0=sQuery(id+"F0.wireOp",EDGE,"E12.MirrorCS");var subQ1=sQuery(id+"F0.wireOp",EDGE,"E0.left");var subQ2=makeQuery(id+"F0.imprint","INTERSECT",VERTEX,{"derivedFrom":[subQ1,subQ0]});Q61=makeQuery(id+"F0.imprint","IMPRINT",FACE,{"disambiguationData":[TD([[makeQuery(id+"F0.imprint","IMPRINT",EDGE,{"disambiguationData":[TD([[subQ2,-1.0]])],"derivedFrom":subQ1}),-1.0]])]});}
            var Q62;
            {var subQ0=sQuery(id+"F0.wireOp",EDGE,"E14.MirrorCS");var subQ1=sQuery(id+"F0.wireOp",EDGE,"E0.left");var subQ2=makeQuery(id+"F0.imprint","INTERSECT",VERTEX,{"derivedFrom":[subQ1,subQ0]});Q62=makeQuery(id+"F0.imprint","IMPRINT",FACE,{"disambiguationData":[TD([[makeQuery(id+"F0.imprint","IMPRINT",EDGE,{"disambiguationData":[TD([[subQ2,-1.0]])],"derivedFrom":subQ1}),-1.0]])]});}
            var Q63;
            {var subQ0=sQuery(id+"F0.wireOp",EDGE,"E7.bottom");var subQ1=sQuery(id+"F0.wireOp",EDGE,"E5");var subQ2=makeQuery(id+"F0.imprint","INTERSECT",VERTEX,{"disambiguationData":[OD(0.0)],"derivedFrom":[subQ1,subQ0]});Q63=makeQuery(id+"F0.imprint","IMPRINT",FACE,{"disambiguationData":[TD([[makeQuery(id+"F0.imprint","IMPRINT",EDGE,{"disambiguationData":[TD([[subQ2,-1.0]])],"derivedFrom":subQ1}),1.0]])]});}
            var Q64;
            {var subQ0=sQuery(id+"F0.wireOp",EDGE,"E17.MirrorCS");var subQ1=sQuery(id+"F0.wireOp",EDGE,"E7.bottom");var subQ2=makeQuery(id+"F0.imprint","INTERSECT",VERTEX,{"derivedFrom":[subQ1,subQ0]});Q64=makeQuery(id+"F0.imprint","IMPRINT",FACE,{"disambiguationData":[TD([[makeQuery(id+"F0.imprint","IMPRINT",EDGE,{"disambiguationData":[TD([[subQ2,-1.0]])],"derivedFrom":subQ1}),-1.0]])]});}
            var Q65;
            {var subQ0=sQuery(id+"F0.wireOp",EDGE,"E16.MirrorCS");var subQ1=sQuery(id+"F0.wireOp",EDGE,"E7.bottom");var subQ2=makeQuery(id+"F0.imprint","INTERSECT",VERTEX,{"derivedFrom":[subQ1,subQ0]});Q65=makeQuery(id+"F0.imprint","IMPRINT",FACE,{"disambiguationData":[TD([[makeQuery(id+"F0.imprint","IMPRINT",EDGE,{"disambiguationData":[TD([[subQ2,-1.0]])],"derivedFrom":subQ1}),-1.0]])]});}
            var Q66;
            {var subQ0=sQuery(id+"F0.wireOp",EDGE,"E16.MirrorCS");var subQ1=sQuery(id+"F0.wireOp",EDGE,"E7.top");var subQ2=makeQuery(id+"F0.imprint","INTERSECT",VERTEX,{"derivedFrom":[subQ1,subQ0]});Q66=makeQuery(id+"F0.imprint","IMPRINT",FACE,{"disambiguationData":[TD([[makeQuery(id+"F0.imprint","IMPRINT",EDGE,{"disambiguationData":[TD([[subQ2,-1.0]])],"derivedFrom":subQ1}),-1.0]])]});}
            var Q67;
            {var subQ0=sQuery(id+"F0.wireOp",EDGE,"E16.MirrorCS");var subQ1=sQuery(id+"F0.wireOp",EDGE,"E6.bottom");var subQ2=makeQuery(id+"F0.imprint","INTERSECT",VERTEX,{"derivedFrom":[subQ1,subQ0]});Q67=makeQuery(id+"F0.imprint","IMPRINT",FACE,{"disambiguationData":[TD([[makeQuery(id+"F0.imprint","IMPRINT",EDGE,{"disambiguationData":[TD([[subQ2,-1.0]])],"derivedFrom":subQ1}),-1.0]])]});}
            var Q68;
            {var subQ0=sQuery(id+"F0.wireOp",EDGE,"E8.bottom");var subQ1=sQuery(id+"F0.wireOp",EDGE,"E5");var subQ2=makeQuery(id+"F0.imprint","INTERSECT",VERTEX,{"disambiguationData":[OD(0.0)],"derivedFrom":[subQ1,subQ0]});Q68=makeQuery(id+"F0.imprint","IMPRINT",FACE,{"disambiguationData":[TD([[makeQuery(id+"F0.imprint","IMPRINT",EDGE,{"disambiguationData":[TD([[subQ2,-1.0]])],"derivedFrom":subQ1}),1.0]])]});}
            var Q69;
            {var subQ0=sQuery(id+"F0.wireOp",EDGE,"E16.MirrorCS");var subQ1=sQuery(id+"F0.wireOp",EDGE,"E8.bottom");var subQ2=makeQuery(id+"F0.imprint","INTERSECT",VERTEX,{"derivedFrom":[subQ1,subQ0]});Q69=makeQuery(id+"F0.imprint","IMPRINT",FACE,{"disambiguationData":[TD([[makeQuery(id+"F0.imprint","IMPRINT",EDGE,{"disambiguationData":[TD([[subQ2,-1.0]])],"derivedFrom":subQ1}),-1.0]])]});}
            var Q70;
            {var subQ0=sQuery(id+"F0.wireOp",EDGE,"E17.MirrorCS");var subQ1=sQuery(id+"F0.wireOp",EDGE,"E8.top");var subQ2=makeQuery(id+"F0.imprint","INTERSECT",VERTEX,{"derivedFrom":[subQ1,subQ0]});Q70=makeQuery(id+"F0.imprint","IMPRINT",FACE,{"disambiguationData":[TD([[makeQuery(id+"F0.imprint","IMPRINT",EDGE,{"disambiguationData":[TD([[subQ2,1.0]])],"derivedFrom":subQ1}),1.0]])]});}
            var Q71;
            {var subQ0=sQuery(id+"F0.wireOp",EDGE,"E16.MirrorCS");var subQ1=sQuery(id+"F0.wireOp",EDGE,"E5");var subQ2=makeQuery(id+"F0.imprint","INTERSECT",VERTEX,{"disambiguationData":[OD(0.0)],"derivedFrom":[subQ1,subQ0]});Q71=makeQuery(id+"F0.imprint","IMPRINT",FACE,{"disambiguationData":[TD([[makeQuery(id+"F0.imprint","IMPRINT",EDGE,{"disambiguationData":[TD([[subQ2,-1.0]])],"derivedFrom":subQ1}),1.0]])]});}
            var Q72;
            {var subQ3=sQuery(id+"F0.wireOp",EDGE,"E17.MirrorCS");var subQ5=sQuery(id+"F0.wireOp",EDGE,"E8.top");var subQ6=makeQuery(id+"F0.imprint","INTERSECT",VERTEX,{"derivedFrom":[subQ5,subQ3]});Q72=makeQuery(id+"F0.imprint","IMPRINT",FACE,{"disambiguationData":[TD([[makeQuery(id+"F0.imprint","IMPRINT",EDGE,{"disambiguationData":[TD([[subQ6,-1.0]])],"derivedFrom":subQ5}),1.0]])]});}
            var Q73;
            {var subQ0=sQuery(id+"F0.wireOp",EDGE,"E18.MirrorCS");var subQ1=sQuery(id+"F0.wireOp",EDGE,"E8.bottom");var subQ2=makeQuery(id+"F0.imprint","INTERSECT",VERTEX,{"derivedFrom":[subQ1,subQ0]});Q73=makeQuery(id+"F0.imprint","IMPRINT",FACE,{"disambiguationData":[TD([[makeQuery(id+"F0.imprint","IMPRINT",EDGE,{"disambiguationData":[TD([[subQ2,-1.0]])],"derivedFrom":subQ1}),-1.0]])]});}
            var Q74;
            {var subQ0=sQuery(id+"F0.wireOp",EDGE,"E18.MirrorCS");var subQ1=sQuery(id+"F0.wireOp",EDGE,"E5");var subQ2=makeQuery(id+"F0.imprint","INTERSECT",VERTEX,{"disambiguationData":[OD(0.0)],"derivedFrom":[subQ1,subQ0]});Q74=makeQuery(id+"F0.imprint","IMPRINT",FACE,{"disambiguationData":[TD([[makeQuery(id+"F0.imprint","IMPRINT",EDGE,{"disambiguationData":[TD([[subQ2,-1.0]])],"derivedFrom":subQ1}),1.0]])]});}
            var Q75;
            {var subQ3=sQuery(id+"F0.wireOp",EDGE,"E18.MirrorCS");var subQ5=sQuery(id+"F0.wireOp",EDGE,"E8.bottom");var subQ6=makeQuery(id+"F0.imprint","INTERSECT",VERTEX,{"derivedFrom":[subQ5,subQ3]});Q75=makeQuery(id+"F0.imprint","IMPRINT",FACE,{"disambiguationData":[TD([[makeQuery(id+"F0.imprint","IMPRINT",EDGE,{"disambiguationData":[TD([[subQ6,-1.0]])],"derivedFrom":subQ5}),1.0]])]});}
            var Q76;
            {var subQ0=sQuery(id+"F0.wireOp",EDGE,"E20.MirrorCS");var subQ1=sQuery(id+"F0.wireOp",EDGE,"E7.top");var subQ2=makeQuery(id+"F0.imprint","INTERSECT",VERTEX,{"derivedFrom":[subQ1,subQ0]});Q76=makeQuery(id+"F0.imprint","IMPRINT",FACE,{"disambiguationData":[TD([[makeQuery(id+"F0.imprint","IMPRINT",EDGE,{"disambiguationData":[TD([[subQ2,-1.0]])],"derivedFrom":subQ1}),-1.0]])]});}
            var Q77;
            {var subQ0=sQuery(id+"F0.wireOp",EDGE,"E22.MirrorCS");var subQ1=sQuery(id+"F0.wireOp",EDGE,"E7.top");var subQ2=makeQuery(id+"F0.imprint","INTERSECT",VERTEX,{"derivedFrom":[subQ1,subQ0]});Q77=makeQuery(id+"F0.imprint","IMPRINT",FACE,{"disambiguationData":[TD([[makeQuery(id+"F0.imprint","IMPRINT",EDGE,{"disambiguationData":[TD([[subQ2,-1.0]])],"derivedFrom":subQ1}),-1.0]])]});}
            var Q78;
            {var subQ0=sQuery(id+"F0.wireOp",EDGE,"E24.MirrorCS");var subQ1=sQuery(id+"F0.wireOp",EDGE,"E5");var subQ2=makeQuery(id+"F0.imprint","INTERSECT",VERTEX,{"disambiguationData":[OD(0.0)],"derivedFrom":[subQ1,subQ0]});Q78=makeQuery(id+"F0.imprint","IMPRINT",FACE,{"disambiguationData":[TD([[makeQuery(id+"F0.imprint","IMPRINT",EDGE,{"disambiguationData":[TD([[subQ2,-1.0]])],"derivedFrom":subQ1}),1.0]])]});}
            var Q79;
            {var subQ0=sQuery(id+"F0.wireOp",EDGE,"E25.MirrorCS");var subQ1=sQuery(id+"F0.wireOp",EDGE,"E8.bottom");var subQ2=makeQuery(id+"F0.imprint","INTERSECT",VERTEX,{"derivedFrom":[subQ1,subQ0]});Q79=makeQuery(id+"F0.imprint","IMPRINT",FACE,{"disambiguationData":[TD([[makeQuery(id+"F0.imprint","IMPRINT",EDGE,{"disambiguationData":[TD([[subQ2,-1.0]])],"derivedFrom":subQ1}),-1.0]])]});}
            var Q80;
            {var subQ0=sQuery(id+"F0.wireOp",EDGE,"E25.MirrorCS");var subQ1=sQuery(id+"F0.wireOp",EDGE,"E7.bottom");var subQ2=makeQuery(id+"F0.imprint","INTERSECT",VERTEX,{"derivedFrom":[subQ1,subQ0]});Q80=makeQuery(id+"F0.imprint","IMPRINT",FACE,{"disambiguationData":[TD([[makeQuery(id+"F0.imprint","IMPRINT",EDGE,{"disambiguationData":[TD([[subQ2,-1.0]])],"derivedFrom":subQ1}),-1.0]])]});}
            var Q81;
            {var subQ0=sQuery(id+"F0.wireOp",EDGE,"E23.MirrorCS");var subQ1=sQuery(id+"F0.wireOp",EDGE,"E6.bottom");var subQ2=makeQuery(id+"F0.imprint","INTERSECT",VERTEX,{"derivedFrom":[subQ1,subQ0]});Q81=makeQuery(id+"F0.imprint","IMPRINT",FACE,{"disambiguationData":[TD([[makeQuery(id+"F0.imprint","IMPRINT",EDGE,{"disambiguationData":[TD([[subQ2,-1.0]])],"derivedFrom":subQ1}),1.0]])]});}
            var Q82;
            {var subQ0=sQuery(id+"F0.wireOp",EDGE,"E24.MirrorCS");var subQ1=sQuery(id+"F0.wireOp",EDGE,"E6.top");var subQ2=makeQuery(id+"F0.imprint","INTERSECT",VERTEX,{"derivedFrom":[subQ1,subQ0]});Q82=makeQuery(id+"F0.imprint","IMPRINT",FACE,{"disambiguationData":[TD([[makeQuery(id+"F0.imprint","IMPRINT",EDGE,{"disambiguationData":[TD([[subQ2,-1.0]])],"derivedFrom":subQ1}),1.0]])]});}
            var Q83;
            {var subQ0=sQuery(id+"F0.wireOp",EDGE,"E25.MirrorCS");var subQ1=sQuery(id+"F0.wireOp",EDGE,"E6.bottom");var subQ2=makeQuery(id+"F0.imprint","INTERSECT",VERTEX,{"derivedFrom":[subQ1,subQ0]});Q83=makeQuery(id+"F0.imprint","IMPRINT",FACE,{"disambiguationData":[TD([[makeQuery(id+"F0.imprint","IMPRINT",EDGE,{"disambiguationData":[TD([[subQ2,-1.0]])],"derivedFrom":subQ1}),1.0]])]});}
            var Q84;
            {var subQ0=sQuery(id+"F0.wireOp",EDGE,"E24.MirrorCS");var subQ1=sQuery(id+"F0.wireOp",EDGE,"E11.MirrorCS");var subQ2=makeQuery(id+"F0.imprint","INTERSECT",VERTEX,{"derivedFrom":[subQ1,subQ0]});Q84=makeQuery(id+"F0.imprint","IMPRINT",FACE,{"disambiguationData":[TD([[makeQuery(id+"F0.imprint","IMPRINT",EDGE,{"disambiguationData":[TD([[subQ2,-1.0]])],"derivedFrom":subQ1}),1.0]])]});}
            var Q85;
            {var subQ0=sQuery(id+"F0.wireOp",EDGE,"E23.MirrorCS");var subQ1=sQuery(id+"F0.wireOp",EDGE,"E12.MirrorCS");var subQ2=makeQuery(id+"F0.imprint","INTERSECT",VERTEX,{"derivedFrom":[subQ1,subQ0]});Q85=makeQuery(id+"F0.imprint","IMPRINT",FACE,{"disambiguationData":[TD([[makeQuery(id+"F0.imprint","IMPRINT",EDGE,{"disambiguationData":[TD([[subQ2,-1.0]])],"derivedFrom":subQ1}),1.0]])]});}
            var Q86;
            {var subQ0=sQuery(id+"F0.wireOp",EDGE,"E25.MirrorCS");var subQ1=sQuery(id+"F0.wireOp",EDGE,"E12.MirrorCS");var subQ2=makeQuery(id+"F0.imprint","INTERSECT",VERTEX,{"derivedFrom":[subQ1,subQ0]});Q86=makeQuery(id+"F0.imprint","IMPRINT",FACE,{"disambiguationData":[TD([[makeQuery(id+"F0.imprint","IMPRINT",EDGE,{"disambiguationData":[TD([[subQ2,-1.0]])],"derivedFrom":subQ1}),1.0]])]});}
            var Q87;
            {var subQ0=sQuery(id+"F0.wireOp",EDGE,"E21.MirrorCS");var subQ1=sQuery(id+"F0.wireOp",EDGE,"E6.bottom");var subQ2=makeQuery(id+"F0.imprint","INTERSECT",VERTEX,{"derivedFrom":[subQ1,subQ0]});Q87=makeQuery(id+"F0.imprint","IMPRINT",FACE,{"disambiguationData":[TD([[makeQuery(id+"F0.imprint","IMPRINT",EDGE,{"disambiguationData":[TD([[subQ2,-1.0]])],"derivedFrom":subQ1}),1.0]])]});}
            var Q88;
            {var subQ3=sQuery(id+"F0.wireOp",EDGE,"E20.MirrorCS");var subQ5=sQuery(id+"F0.wireOp",EDGE,"E7.bottom");var subQ6=makeQuery(id+"F0.imprint","INTERSECT",VERTEX,{"derivedFrom":[subQ5,subQ3]});Q88=makeQuery(id+"F0.imprint","IMPRINT",FACE,{"disambiguationData":[TD([[makeQuery(id+"F0.imprint","IMPRINT",EDGE,{"disambiguationData":[TD([[subQ6,-1.0]])],"derivedFrom":subQ5}),1.0]])]});}
            var Q89;
            {var subQ0=sQuery(id+"F0.wireOp",EDGE,"E21.MirrorCS");var subQ1=sQuery(id+"F0.wireOp",EDGE,"E6.bottom");var subQ2=makeQuery(id+"F0.imprint","INTERSECT",VERTEX,{"derivedFrom":[subQ1,subQ0]});Q89=makeQuery(id+"F0.imprint","IMPRINT",FACE,{"disambiguationData":[TD([[makeQuery(id+"F0.imprint","IMPRINT",EDGE,{"disambiguationData":[TD([[subQ2,1.0]])],"derivedFrom":subQ1}),1.0]])]});}
            var Q90;
            {var subQ0=sQuery(id+"F0.wireOp",EDGE,"E19.MirrorCS");var subQ5=sQuery(id+"F0.wireOp",EDGE,"E6.top");var subQ6=makeQuery(id+"F0.imprint","INTERSECT",VERTEX,{"derivedFrom":[subQ5,subQ0]});Q90=makeQuery(id+"F0.imprint","IMPRINT",FACE,{"disambiguationData":[TD([[makeQuery(id+"F0.imprint","IMPRINT",EDGE,{"disambiguationData":[TD([[subQ6,-1.0]])],"derivedFrom":subQ5}),-1.0]])]});}
            var Q91;
            {var subQ0=sQuery(id+"F0.wireOp",EDGE,"E18.MirrorCS");var subQ1=sQuery(id+"F0.wireOp",EDGE,"E6.top");var subQ2=makeQuery(id+"F0.imprint","INTERSECT",VERTEX,{"derivedFrom":[subQ1,subQ0]});Q91=makeQuery(id+"F0.imprint","IMPRINT",FACE,{"disambiguationData":[TD([[makeQuery(id+"F0.imprint","IMPRINT",EDGE,{"disambiguationData":[TD([[subQ2,-1.0]])],"derivedFrom":subQ1}),1.0]])]});}
            var Q92;
            {var subQ0=sQuery(id+"F0.wireOp",EDGE,"E18.MirrorCS");var subQ1=sQuery(id+"F0.wireOp",EDGE,"E6.bottom");var subQ2=makeQuery(id+"F0.imprint","INTERSECT",VERTEX,{"derivedFrom":[subQ1,subQ0]});Q92=makeQuery(id+"F0.imprint","IMPRINT",FACE,{"disambiguationData":[TD([[makeQuery(id+"F0.imprint","IMPRINT",EDGE,{"disambiguationData":[TD([[subQ2,-1.0]])],"derivedFrom":subQ1}),1.0]])]});}
            var Q93;
            {var subQ0=sQuery(id+"F0.wireOp",EDGE,"E17.MirrorCS");var subQ1=sQuery(id+"F0.wireOp",EDGE,"E6.bottom");var subQ2=makeQuery(id+"F0.imprint","INTERSECT",VERTEX,{"derivedFrom":[subQ1,subQ0]});Q93=makeQuery(id+"F0.imprint","IMPRINT",FACE,{"disambiguationData":[TD([[makeQuery(id+"F0.imprint","IMPRINT",EDGE,{"disambiguationData":[TD([[subQ2,-1.0]])],"derivedFrom":subQ1}),1.0]])]});}
            var Q94;
            {var subQ3=sQuery(id+"F0.wireOp",EDGE,"E19.MirrorCS");var subQ5=sQuery(id+"F0.wireOp",EDGE,"E7.top");var subQ6=makeQuery(id+"F0.imprint","INTERSECT",VERTEX,{"derivedFrom":[subQ5,subQ3]});Q94=makeQuery(id+"F0.imprint","IMPRINT",FACE,{"disambiguationData":[TD([[makeQuery(id+"F0.imprint","IMPRINT",EDGE,{"disambiguationData":[TD([[subQ6,-1.0]])],"derivedFrom":subQ5}),1.0]])]});}
            var Q95;
            {var subQ0=sQuery(id+"F0.wireOp",EDGE,"E21.MirrorCS");var subQ1=sQuery(id+"F0.wireOp",EDGE,"E7.bottom");var subQ2=makeQuery(id+"F0.imprint","INTERSECT",VERTEX,{"derivedFrom":[subQ1,subQ0]});Q95=makeQuery(id+"F0.imprint","IMPRINT",FACE,{"disambiguationData":[TD([[makeQuery(id+"F0.imprint","IMPRINT",EDGE,{"disambiguationData":[TD([[subQ2,-1.0]])],"derivedFrom":subQ1}),-1.0]])]});}
            var Q96;
            {var subQ0=sQuery(id+"F0.wireOp",EDGE,"E24.MirrorCS");var subQ1=sQuery(id+"F0.wireOp",EDGE,"E6.bottom");var subQ2=makeQuery(id+"F0.imprint","INTERSECT",VERTEX,{"derivedFrom":[subQ1,subQ0]});Q96=makeQuery(id+"F0.imprint","IMPRINT",FACE,{"disambiguationData":[TD([[makeQuery(id+"F0.imprint","IMPRINT",EDGE,{"disambiguationData":[TD([[subQ2,-1.0]])],"derivedFrom":subQ1}),-1.0]])]});}
            var Q97;
            {var subQ0=sQuery(id+"F0.wireOp",EDGE,"E25.MirrorCS");var subQ1=sQuery(id+"F0.wireOp",EDGE,"E10.MirrorCS");var subQ2=makeQuery(id+"F0.imprint","INTERSECT",VERTEX,{"derivedFrom":[subQ1,subQ0]});Q97=makeQuery(id+"F0.imprint","IMPRINT",FACE,{"disambiguationData":[TD([[makeQuery(id+"F0.imprint","IMPRINT",EDGE,{"disambiguationData":[TD([[subQ2,-1.0]])],"derivedFrom":subQ1}),1.0]])]});}
            var Q98;
            {var subQ0=sQuery(id+"F0.wireOp",EDGE,"E27.MirrorCS");var subQ1=sQuery(id+"F0.wireOp",EDGE,"E5");var subQ2=makeQuery(id+"F0.imprint","INTERSECT",VERTEX,{"disambiguationData":[OD(1.0)],"derivedFrom":[subQ1,subQ0]});Q98=makeQuery(id+"F0.imprint","IMPRINT",FACE,{"disambiguationData":[TD([[makeQuery(id+"F0.imprint","IMPRINT",EDGE,{"disambiguationData":[TD([[subQ2,-1.0]])],"derivedFrom":subQ1}),1.0]])]});}
            var Q99;
            {var subQ0=sQuery(id+"F0.wireOp",EDGE,"E14.MirrorCS");var subQ1=sQuery(id+"F0.wireOp",EDGE,"E5");var subQ2=makeQuery(id+"F0.imprint","INTERSECT",VERTEX,{"disambiguationData":[OD(0.0)],"derivedFrom":[subQ1,subQ0]});Q99=makeQuery(id+"F0.imprint","IMPRINT",FACE,{"disambiguationData":[TD([[makeQuery(id+"F0.imprint","IMPRINT",EDGE,{"disambiguationData":[TD([[subQ2,-1.0]])],"derivedFrom":subQ1}),1.0]])]});}
            var Q100;
            {var subQ0=sQuery(id+"F0.wireOp",EDGE,"E26.MirrorCS");var subQ1=sQuery(id+"F0.wireOp",EDGE,"E14.MirrorCS");var subQ2=makeQuery(id+"F0.imprint","INTERSECT",VERTEX,{"derivedFrom":[subQ1,subQ0]});Q100=makeQuery(id+"F0.imprint","IMPRINT",FACE,{"disambiguationData":[TD([[makeQuery(id+"F0.imprint","IMPRINT",EDGE,{"disambiguationData":[TD([[subQ2,-1.0]])],"derivedFrom":subQ1}),1.0]])]});}
            var Q101;
            {var subQ0=sQuery(id+"F0.wireOp",EDGE,"E23.MirrorCS");var subQ1=sQuery(id+"F0.wireOp",EDGE,"E5");var subQ2=makeQuery(id+"F0.imprint","INTERSECT",VERTEX,{"disambiguationData":[OD(1.0)],"derivedFrom":[subQ1,subQ0]});Q101=makeQuery(id+"F0.imprint","IMPRINT",FACE,{"disambiguationData":[TD([[makeQuery(id+"F0.imprint","IMPRINT",EDGE,{"disambiguationData":[TD([[subQ2,-1.0]])],"derivedFrom":subQ1}),1.0]])]});}
            var Q102;
            {var subQ0=sQuery(id+"F0.wireOp",EDGE,"E21.MirrorCS");var subQ1=sQuery(id+"F0.wireOp",EDGE,"E5");var subQ2=makeQuery(id+"F0.imprint","INTERSECT",VERTEX,{"disambiguationData":[OD(1.0)],"derivedFrom":[subQ1,subQ0]});Q102=makeQuery(id+"F0.imprint","IMPRINT",FACE,{"disambiguationData":[TD([[makeQuery(id+"F0.imprint","IMPRINT",EDGE,{"disambiguationData":[TD([[subQ2,-1.0]])],"derivedFrom":subQ1}),1.0]])]});}
            var Q103;
            {var subQ0=sQuery(id+"F0.wireOp",EDGE,"E20.MirrorCS");var subQ1=sQuery(id+"F0.wireOp",EDGE,"E14.MirrorCS");var subQ2=makeQuery(id+"F0.imprint","INTERSECT",VERTEX,{"derivedFrom":[subQ1,subQ0]});Q103=makeQuery(id+"F0.imprint","IMPRINT",FACE,{"disambiguationData":[TD([[makeQuery(id+"F0.imprint","IMPRINT",EDGE,{"disambiguationData":[TD([[subQ2,-1.0]])],"derivedFrom":subQ1}),1.0]])]});}
            var Q104;
            {var subQ0=sQuery(id+"F0.wireOp",EDGE,"E21.MirrorCS");var subQ1=sQuery(id+"F0.wireOp",EDGE,"E14.MirrorCS");var subQ2=makeQuery(id+"F0.imprint","INTERSECT",VERTEX,{"derivedFrom":[subQ1,subQ0]});Q104=makeQuery(id+"F0.imprint","IMPRINT",FACE,{"disambiguationData":[TD([[makeQuery(id+"F0.imprint","IMPRINT",EDGE,{"disambiguationData":[TD([[subQ2,-1.0]])],"derivedFrom":subQ1}),1.0]])]});}
            var Q105;
            {var subQ0=sQuery(id+"F0.wireOp",EDGE,"E17.MirrorCS");var subQ1=sQuery(id+"F0.wireOp",EDGE,"E5");var subQ2=makeQuery(id+"F0.imprint","INTERSECT",VERTEX,{"disambiguationData":[OD(1.0)],"derivedFrom":[subQ1,subQ0]});Q105=makeQuery(id+"F0.imprint","IMPRINT",FACE,{"disambiguationData":[TD([[makeQuery(id+"F0.imprint","IMPRINT",EDGE,{"disambiguationData":[TD([[subQ2,-1.0]])],"derivedFrom":subQ1}),1.0]])]});}
            var Q106;
            {var subQ0=sQuery(id+"F0.wireOp",EDGE,"E16.MirrorCS");var subQ1=sQuery(id+"F0.wireOp",EDGE,"E13.MirrorCS");var subQ2=makeQuery(id+"F0.imprint","INTERSECT",VERTEX,{"derivedFrom":[subQ1,subQ0]});Q106=makeQuery(id+"F0.imprint","IMPRINT",FACE,{"disambiguationData":[TD([[makeQuery(id+"F0.imprint","IMPRINT",EDGE,{"disambiguationData":[TD([[subQ2,-1.0]])],"derivedFrom":subQ1}),1.0]])]});}
            var Q107;
            {var subQ0=sQuery(id+"F0.wireOp",EDGE,"E13.MirrorCS");var subQ1=sQuery(id+"F0.wireOp",EDGE,"E5");var subQ2=makeQuery(id+"F0.imprint","INTERSECT",VERTEX,{"disambiguationData":[OD(1.0)],"derivedFrom":[subQ1,subQ0]});Q107=makeQuery(id+"F0.imprint","IMPRINT",FACE,{"disambiguationData":[TD([[makeQuery(id+"F0.imprint","IMPRINT",EDGE,{"disambiguationData":[TD([[subQ2,-1.0]])],"derivedFrom":subQ1}),1.0]])]});}
            var Q108;
            {var subQ0=sQuery(id+"F0.wireOp",EDGE,"E16.MirrorCS");var subQ1=sQuery(id+"F0.wireOp",EDGE,"E12.MirrorCS");var subQ2=makeQuery(id+"F0.imprint","INTERSECT",VERTEX,{"derivedFrom":[subQ1,subQ0]});Q108=makeQuery(id+"F0.imprint","IMPRINT",FACE,{"disambiguationData":[TD([[makeQuery(id+"F0.imprint","IMPRINT",EDGE,{"disambiguationData":[TD([[subQ2,-1.0]])],"derivedFrom":subQ1}),1.0]])]});}
            var Q109;
            {var subQ0=sQuery(id+"F0.wireOp",EDGE,"E16.MirrorCS");var subQ1=sQuery(id+"F0.wireOp",EDGE,"E11.MirrorCS");var subQ2=makeQuery(id+"F0.imprint","INTERSECT",VERTEX,{"derivedFrom":[subQ1,subQ0]});Q109=makeQuery(id+"F0.imprint","IMPRINT",FACE,{"disambiguationData":[TD([[makeQuery(id+"F0.imprint","IMPRINT",EDGE,{"disambiguationData":[TD([[subQ2,-1.0]])],"derivedFrom":subQ1}),1.0]])]});}
            var Q110;
            {var subQ0=sQuery(id+"F0.wireOp",EDGE,"E17.MirrorCS");var subQ1=sQuery(id+"F0.wireOp",EDGE,"E12.MirrorCS");var subQ2=makeQuery(id+"F0.imprint","INTERSECT",VERTEX,{"derivedFrom":[subQ1,subQ0]});Q110=makeQuery(id+"F0.imprint","IMPRINT",FACE,{"disambiguationData":[TD([[makeQuery(id+"F0.imprint","IMPRINT",EDGE,{"disambiguationData":[TD([[subQ2,-1.0]])],"derivedFrom":subQ1}),1.0]])]});}
            var Q111;
            {var subQ0=sQuery(id+"F0.wireOp",EDGE,"E19.MirrorCS");var subQ1=sQuery(id+"F0.wireOp",EDGE,"E10.MirrorCS");var subQ2=makeQuery(id+"F0.imprint","INTERSECT",VERTEX,{"derivedFrom":[subQ1,subQ0]});Q111=makeQuery(id+"F0.imprint","IMPRINT",FACE,{"disambiguationData":[TD([[makeQuery(id+"F0.imprint","IMPRINT",EDGE,{"disambiguationData":[TD([[subQ2,-1.0]])],"derivedFrom":subQ1}),1.0]])]});}
            var Q112;
            {var subQ0=sQuery(id+"F0.wireOp",EDGE,"E16.MirrorCS");var subQ1=sQuery(id+"F0.wireOp",EDGE,"E10.MirrorCS");var subQ2=makeQuery(id+"F0.imprint","INTERSECT",VERTEX,{"derivedFrom":[subQ1,subQ0]});Q112=makeQuery(id+"F0.imprint","IMPRINT",FACE,{"disambiguationData":[TD([[makeQuery(id+"F0.imprint","IMPRINT",EDGE,{"disambiguationData":[TD([[subQ2,-1.0]])],"derivedFrom":subQ1}),1.0]])]});}
            var Q113;
            {var subQ0=sQuery(id+"F0.wireOp",EDGE,"E11.MirrorCS");var subQ1=sQuery(id+"F0.wireOp",EDGE,"E5");var subQ2=makeQuery(id+"F0.imprint","INTERSECT",VERTEX,{"disambiguationData":[OD(1.0)],"derivedFrom":[subQ1,subQ0]});Q113=makeQuery(id+"F0.imprint","IMPRINT",FACE,{"disambiguationData":[TD([[makeQuery(id+"F0.imprint","IMPRINT",EDGE,{"disambiguationData":[TD([[subQ2,-1.0]])],"derivedFrom":subQ1}),1.0]])]});}
            var Q114;
            {var subQ0=sQuery(id+"F0.wireOp",EDGE,"E6.bottom");var subQ1=sQuery(id+"F0.wireOp",EDGE,"E5");var subQ2=makeQuery(id+"F0.imprint","INTERSECT",VERTEX,{"disambiguationData":[OD(0.0)],"derivedFrom":[subQ1,subQ0]});Q114=makeQuery(id+"F0.imprint","IMPRINT",FACE,{"disambiguationData":[TD([[makeQuery(id+"F0.imprint","IMPRINT",EDGE,{"disambiguationData":[TD([[subQ2,1.0]])],"derivedFrom":subQ1}),1.0]])]});}
            var Q115;
            Q115=makeQuery(id+"F0.imprint","IMPRINT",FACE,{"disambiguationData":[TD([[makeQuery(id+"F0.imprint","IMPRINT",EDGE,{"derivedFrom":sQuery(id+"F0.wireOp",EDGE,"E4.MirrorC")}),-1.0]])]});
            var Q116;
            {var subQ0=sQuery(id+"F0.wireOp",EDGE,"E16.MirrorCS");var subQ1=sQuery(id+"F0.wireOp",EDGE,"E0.top");var subQ2=makeQuery(id+"F0.imprint","INTERSECT",VERTEX,{"derivedFrom":[subQ1,subQ0]});Q116=makeQuery(id+"F0.imprint","IMPRINT",FACE,{"disambiguationData":[TD([[makeQuery(id+"F0.imprint","IMPRINT",EDGE,{"disambiguationData":[TD([[subQ2,-1.0]])],"derivedFrom":subQ1}),-1.0]])]});}
            var Q117;
            {var subQ0=sQuery(id+"F0.wireOp",EDGE,"E19.MirrorCS");var subQ1=sQuery(id+"F0.wireOp",EDGE,"E0.top");var subQ2=makeQuery(id+"F0.imprint","INTERSECT",VERTEX,{"derivedFrom":[subQ1,subQ0]});Q117=makeQuery(id+"F0.imprint","IMPRINT",FACE,{"disambiguationData":[TD([[makeQuery(id+"F0.imprint","IMPRINT",EDGE,{"disambiguationData":[TD([[subQ2,-1.0]])],"derivedFrom":subQ1}),-1.0]])]});}
            var Q118;
            {var subQ0=sQuery(id+"F0.wireOp",EDGE,"E20.MirrorCS");var subQ1=sQuery(id+"F0.wireOp",EDGE,"E0.top");var subQ2=makeQuery(id+"F0.imprint","INTERSECT",VERTEX,{"derivedFrom":[subQ1,subQ0]});Q118=makeQuery(id+"F0.imprint","IMPRINT",FACE,{"disambiguationData":[TD([[makeQuery(id+"F0.imprint","IMPRINT",EDGE,{"disambiguationData":[TD([[subQ2,-1.0]])],"derivedFrom":subQ1}),-1.0]])]});}
            var Q119;
            {var subQ0=sQuery(id+"F0.wireOp",EDGE,"E21.MirrorCS");var subQ1=sQuery(id+"F0.wireOp",EDGE,"E0.top");var subQ2=makeQuery(id+"F0.imprint","INTERSECT",VERTEX,{"derivedFrom":[subQ1,subQ0]});Q119=makeQuery(id+"F0.imprint","IMPRINT",FACE,{"disambiguationData":[TD([[makeQuery(id+"F0.imprint","IMPRINT",EDGE,{"disambiguationData":[TD([[subQ2,-1.0]])],"derivedFrom":subQ1}),-1.0]])]});}
            var Q120;
            {var subQ0=sQuery(id+"F0.wireOp",EDGE,"E22.MirrorCS");var subQ1=sQuery(id+"F0.wireOp",EDGE,"E0.top");var subQ2=makeQuery(id+"F0.imprint","INTERSECT",VERTEX,{"derivedFrom":[subQ1,subQ0]});Q120=makeQuery(id+"F0.imprint","IMPRINT",FACE,{"disambiguationData":[TD([[makeQuery(id+"F0.imprint","IMPRINT",EDGE,{"disambiguationData":[TD([[subQ2,-1.0]])],"derivedFrom":subQ1}),-1.0]])]});}
            var Q121;
            {var subQ0=sQuery(id+"F0.wireOp",EDGE,"E21.MirrorCS");var subQ1=sQuery(id+"F0.wireOp",EDGE,"E10.MirrorCS");var subQ2=makeQuery(id+"F0.imprint","INTERSECT",VERTEX,{"derivedFrom":[subQ1,subQ0]});Q121=makeQuery(id+"F0.imprint","IMPRINT",FACE,{"disambiguationData":[TD([[makeQuery(id+"F0.imprint","IMPRINT",EDGE,{"disambiguationData":[TD([[subQ2,-1.0]])],"derivedFrom":subQ1}),1.0]])]});}
            var Q122;
            {var subQ0=sQuery(id+"F0.wireOp",EDGE,"E22.MirrorCS");var subQ1=sQuery(id+"F0.wireOp",EDGE,"E6.top");var subQ2=makeQuery(id+"F0.imprint","INTERSECT",VERTEX,{"derivedFrom":[subQ1,subQ0]});Q122=makeQuery(id+"F0.imprint","IMPRINT",FACE,{"disambiguationData":[TD([[makeQuery(id+"F0.imprint","IMPRINT",EDGE,{"disambiguationData":[TD([[subQ2,-1.0]])],"derivedFrom":subQ1}),1.0]])]});}
            var Q123;
            {var subQ0=sQuery(id+"F0.wireOp",EDGE,"E22.MirrorCS");var subQ1=sQuery(id+"F0.wireOp",EDGE,"E10.MirrorCS");var subQ2=makeQuery(id+"F0.imprint","INTERSECT",VERTEX,{"derivedFrom":[subQ1,subQ0]});Q123=makeQuery(id+"F0.imprint","IMPRINT",FACE,{"disambiguationData":[TD([[makeQuery(id+"F0.imprint","IMPRINT",EDGE,{"disambiguationData":[TD([[subQ2,-1.0]])],"derivedFrom":subQ1}),1.0]])]});}
            var Q124;
            {var subQ0=sQuery(id+"F0.wireOp",EDGE,"E23.MirrorCS");var subQ1=sQuery(id+"F0.wireOp",EDGE,"E10.MirrorCS");var subQ2=makeQuery(id+"F0.imprint","INTERSECT",VERTEX,{"derivedFrom":[subQ1,subQ0]});Q124=makeQuery(id+"F0.imprint","IMPRINT",FACE,{"disambiguationData":[TD([[makeQuery(id+"F0.imprint","IMPRINT",EDGE,{"disambiguationData":[TD([[subQ2,-1.0]])],"derivedFrom":subQ1}),1.0]])]});}
            var Q125;
            {var subQ0=sQuery(id+"F0.wireOp",EDGE,"E22.MirrorCS");var subQ1=sQuery(id+"F0.wireOp",EDGE,"E6.bottom");var subQ2=makeQuery(id+"F0.imprint","INTERSECT",VERTEX,{"derivedFrom":[subQ1,subQ0]});Q125=makeQuery(id+"F0.imprint","IMPRINT",FACE,{"disambiguationData":[TD([[makeQuery(id+"F0.imprint","IMPRINT",EDGE,{"disambiguationData":[TD([[subQ2,-1.0]])],"derivedFrom":subQ1}),-1.0]])]});}
            var Q126;
            {var subQ0=sQuery(id+"F0.wireOp",EDGE,"E23.MirrorCS");var subQ1=sQuery(id+"F0.wireOp",EDGE,"E7.bottom");var subQ2=makeQuery(id+"F0.imprint","INTERSECT",VERTEX,{"derivedFrom":[subQ1,subQ0]});Q126=makeQuery(id+"F0.imprint","IMPRINT",FACE,{"disambiguationData":[TD([[makeQuery(id+"F0.imprint","IMPRINT",EDGE,{"disambiguationData":[TD([[subQ2,-1.0]])],"derivedFrom":subQ1}),-1.0]])]});}
            var Q127;
            {var subQ0=sQuery(id+"F0.wireOp",EDGE,"E24.MirrorCS");var subQ1=sQuery(id+"F0.wireOp",EDGE,"E7.top");var subQ2=makeQuery(id+"F0.imprint","INTERSECT",VERTEX,{"derivedFrom":[subQ1,subQ0]});Q127=makeQuery(id+"F0.imprint","IMPRINT",FACE,{"disambiguationData":[TD([[makeQuery(id+"F0.imprint","IMPRINT",EDGE,{"disambiguationData":[TD([[subQ2,-1.0]])],"derivedFrom":subQ1}),-1.0]])]});}
            var Q128;
            {var subQ0=sQuery(id+"F0.wireOp",EDGE,"E22.MirrorCS");var subQ1=sQuery(id+"F0.wireOp",EDGE,"E5");var subQ2=makeQuery(id+"F0.imprint","INTERSECT",VERTEX,{"disambiguationData":[OD(0.0)],"derivedFrom":[subQ1,subQ0]});Q128=makeQuery(id+"F0.imprint","IMPRINT",FACE,{"disambiguationData":[TD([[makeQuery(id+"F0.imprint","IMPRINT",EDGE,{"disambiguationData":[TD([[subQ2,-1.0]])],"derivedFrom":subQ1}),1.0]])]});}
            var Q129;
            {var subQ0=sQuery(id+"F0.wireOp",EDGE,"E22.MirrorCS");var subQ1=sQuery(id+"F0.wireOp",EDGE,"E8.bottom");var subQ2=makeQuery(id+"F0.imprint","INTERSECT",VERTEX,{"derivedFrom":[subQ1,subQ0]});Q129=makeQuery(id+"F0.imprint","IMPRINT",FACE,{"disambiguationData":[TD([[makeQuery(id+"F0.imprint","IMPRINT",EDGE,{"disambiguationData":[TD([[subQ2,-1.0]])],"derivedFrom":subQ1}),-1.0]])]});}
            var Q130;
            {var subQ0=sQuery(id+"F0.wireOp",EDGE,"E23.MirrorCS");var subQ1=sQuery(id+"F0.wireOp",EDGE,"E8.bottom");var subQ2=makeQuery(id+"F0.imprint","INTERSECT",VERTEX,{"derivedFrom":[subQ1,subQ0]});Q130=makeQuery(id+"F0.imprint","IMPRINT",FACE,{"disambiguationData":[TD([[makeQuery(id+"F0.imprint","IMPRINT",EDGE,{"disambiguationData":[TD([[subQ2,-1.0]])],"derivedFrom":subQ1}),-1.0]])]});}
            var Q131;
            {var subQ0=sQuery(id+"F0.wireOp",EDGE,"E21.MirrorCS");var subQ1=sQuery(id+"F0.wireOp",EDGE,"E8.bottom");var subQ2=makeQuery(id+"F0.imprint","INTERSECT",VERTEX,{"derivedFrom":[subQ1,subQ0]});Q131=makeQuery(id+"F0.imprint","IMPRINT",FACE,{"disambiguationData":[TD([[makeQuery(id+"F0.imprint","IMPRINT",EDGE,{"disambiguationData":[TD([[subQ2,-1.0]])],"derivedFrom":subQ1}),-1.0]])]});}
            var Q132;
            {var subQ0=sQuery(id+"F0.wireOp",EDGE,"E18.MirrorCS");var subQ1=sQuery(id+"F0.wireOp",EDGE,"E6.bottom");var subQ2=makeQuery(id+"F0.imprint","INTERSECT",VERTEX,{"derivedFrom":[subQ1,subQ0]});Q132=makeQuery(id+"F0.imprint","IMPRINT",FACE,{"disambiguationData":[TD([[makeQuery(id+"F0.imprint","IMPRINT",EDGE,{"disambiguationData":[TD([[subQ2,-1.0]])],"derivedFrom":subQ1}),-1.0]])]});}
            var Q133;
            {var subQ0=sQuery(id+"F0.wireOp",EDGE,"E16.MirrorCS");var subQ1=sQuery(id+"F0.wireOp",EDGE,"E6.top");var subQ2=makeQuery(id+"F0.imprint","INTERSECT",VERTEX,{"derivedFrom":[subQ1,subQ0]});Q133=makeQuery(id+"F0.imprint","IMPRINT",FACE,{"disambiguationData":[TD([[makeQuery(id+"F0.imprint","IMPRINT",EDGE,{"disambiguationData":[TD([[subQ2,-1.0]])],"derivedFrom":subQ1}),1.0]])]});}
            var Q134;
            {var subQ0=sQuery(id+"F0.wireOp",EDGE,"E16.MirrorCS");var subQ1=sQuery(id+"F0.wireOp",EDGE,"E6.bottom");var subQ2=makeQuery(id+"F0.imprint","INTERSECT",VERTEX,{"derivedFrom":[subQ1,subQ0]});Q134=makeQuery(id+"F0.imprint","IMPRINT",FACE,{"disambiguationData":[TD([[makeQuery(id+"F0.imprint","IMPRINT",EDGE,{"disambiguationData":[TD([[subQ2,-1.0]])],"derivedFrom":subQ1}),1.0]])]});}
            var Q135;
            {var subQ0=sQuery(id+"F0.wireOp",EDGE,"E17.MirrorCS");var subQ1=sQuery(id+"F0.wireOp",EDGE,"E10.MirrorCS");var subQ2=makeQuery(id+"F0.imprint","INTERSECT",VERTEX,{"derivedFrom":[subQ1,subQ0]});Q135=makeQuery(id+"F0.imprint","IMPRINT",FACE,{"disambiguationData":[TD([[makeQuery(id+"F0.imprint","IMPRINT",EDGE,{"disambiguationData":[TD([[subQ2,-1.0]])],"derivedFrom":subQ1}),1.0]])]});}
            var Q136;
            {var subQ0=sQuery(id+"F0.wireOp",EDGE,"E18.MirrorCS");var subQ1=sQuery(id+"F0.wireOp",EDGE,"E13.MirrorCS");var subQ2=makeQuery(id+"F0.imprint","INTERSECT",VERTEX,{"derivedFrom":[subQ1,subQ0]});Q136=makeQuery(id+"F0.imprint","IMPRINT",FACE,{"disambiguationData":[TD([[makeQuery(id+"F0.imprint","IMPRINT",EDGE,{"disambiguationData":[TD([[subQ2,-1.0]])],"derivedFrom":subQ1}),1.0]])]});}
            var Q137;
            {var subQ0=sQuery(id+"F0.wireOp",EDGE,"E20.MirrorCS");var subQ1=sQuery(id+"F0.wireOp",EDGE,"E10.MirrorCS");var subQ2=makeQuery(id+"F0.imprint","INTERSECT",VERTEX,{"derivedFrom":[subQ1,subQ0]});Q137=makeQuery(id+"F0.imprint","IMPRINT",FACE,{"disambiguationData":[TD([[makeQuery(id+"F0.imprint","IMPRINT",EDGE,{"disambiguationData":[TD([[subQ2,-1.0]])],"derivedFrom":subQ1}),1.0]])]});}
            var Q138;
            {var subQ0=sQuery(id+"F0.wireOp",EDGE,"E20.MirrorCS");var subQ5=sQuery(id+"F0.wireOp",EDGE,"E10.MirrorCS");var subQ6=makeQuery(id+"F0.imprint","INTERSECT",VERTEX,{"derivedFrom":[subQ5,subQ0]});Q138=makeQuery(id+"F0.imprint","IMPRINT",FACE,{"disambiguationData":[TD([[makeQuery(id+"F0.imprint","IMPRINT",EDGE,{"disambiguationData":[TD([[subQ6,-1.0]])],"derivedFrom":subQ5}),-1.0]])]});}
            var Q139;
            {var subQ0=sQuery(id+"F0.wireOp",EDGE,"E26.MirrorCS");var subQ1=sQuery(id+"F0.wireOp",EDGE,"E11.MirrorCS");var subQ2=makeQuery(id+"F0.imprint","INTERSECT",VERTEX,{"derivedFrom":[subQ1,subQ0]});Q139=makeQuery(id+"F0.imprint","IMPRINT",FACE,{"disambiguationData":[TD([[makeQuery(id+"F0.imprint","IMPRINT",EDGE,{"disambiguationData":[TD([[subQ2,-1.0]])],"derivedFrom":subQ1}),1.0]])]});}
            var Q140;
            {var subQ0=sQuery(id+"F0.wireOp",EDGE,"E15.MirrorCS");var subQ1=sQuery(id+"F0.wireOp",EDGE,"E5");var subQ2=makeQuery(id+"F0.imprint","INTERSECT",VERTEX,{"disambiguationData":[OD(1.0)],"derivedFrom":[subQ1,subQ0]});Q140=makeQuery(id+"F0.imprint","IMPRINT",FACE,{"disambiguationData":[TD([[makeQuery(id+"F0.imprint","IMPRINT",EDGE,{"disambiguationData":[TD([[subQ2,-1.0]])],"derivedFrom":subQ1}),1.0]])]});}
            var Q141;
            {var subQ0=sQuery(id+"F0.wireOp",EDGE,"E16.MirrorCS");var subQ1=sQuery(id+"F0.wireOp",EDGE,"E14.MirrorCS");var subQ2=makeQuery(id+"F0.imprint","INTERSECT",VERTEX,{"derivedFrom":[subQ1,subQ0]});Q141=makeQuery(id+"F0.imprint","IMPRINT",FACE,{"disambiguationData":[TD([[makeQuery(id+"F0.imprint","IMPRINT",EDGE,{"disambiguationData":[TD([[subQ2,-1.0]])],"derivedFrom":subQ1}),1.0]])]});}
            var Q142;
            {var subQ0=sQuery(id+"F0.wireOp",EDGE,"E18.MirrorCS");var subQ1=sQuery(id+"F0.wireOp",EDGE,"E12.MirrorCS");var subQ2=makeQuery(id+"F0.imprint","INTERSECT",VERTEX,{"derivedFrom":[subQ1,subQ0]});Q142=makeQuery(id+"F0.imprint","IMPRINT",FACE,{"disambiguationData":[TD([[makeQuery(id+"F0.imprint","IMPRINT",EDGE,{"disambiguationData":[TD([[subQ2,-1.0]])],"derivedFrom":subQ1}),1.0]])]});}
            var Q143;
            {var subQ0=sQuery(id+"F0.wireOp",EDGE,"E18.MirrorCS");var subQ1=sQuery(id+"F0.wireOp",EDGE,"E11.MirrorCS");var subQ2=makeQuery(id+"F0.imprint","INTERSECT",VERTEX,{"derivedFrom":[subQ1,subQ0]});Q143=makeQuery(id+"F0.imprint","IMPRINT",FACE,{"disambiguationData":[TD([[makeQuery(id+"F0.imprint","IMPRINT",EDGE,{"disambiguationData":[TD([[subQ2,-1.0]])],"derivedFrom":subQ1}),1.0]])]});}
            var Q144;
            {var subQ0=sQuery(id+"F0.wireOp",EDGE,"E18.MirrorCS");var subQ1=sQuery(id+"F0.wireOp",EDGE,"E10.MirrorCS");var subQ2=makeQuery(id+"F0.imprint","INTERSECT",VERTEX,{"derivedFrom":[subQ1,subQ0]});Q144=makeQuery(id+"F0.imprint","IMPRINT",FACE,{"disambiguationData":[TD([[makeQuery(id+"F0.imprint","IMPRINT",EDGE,{"disambiguationData":[TD([[subQ2,-1.0]])],"derivedFrom":subQ1}),1.0]])]});}
            var Q145;
            {var subQ0=sQuery(id+"F0.wireOp",EDGE,"E22.MirrorCS");var subQ1=sQuery(id+"F0.wireOp",EDGE,"E14.MirrorCS");var subQ2=makeQuery(id+"F0.imprint","INTERSECT",VERTEX,{"derivedFrom":[subQ1,subQ0]});Q145=makeQuery(id+"F0.imprint","IMPRINT",FACE,{"disambiguationData":[TD([[makeQuery(id+"F0.imprint","IMPRINT",EDGE,{"disambiguationData":[TD([[subQ2,-1.0]])],"derivedFrom":subQ1}),1.0]])]});}
            var Q146;
            {var subQ0=sQuery(id+"F0.wireOp",EDGE,"E24.MirrorCS");var subQ1=sQuery(id+"F0.wireOp",EDGE,"E12.MirrorCS");var subQ2=makeQuery(id+"F0.imprint","INTERSECT",VERTEX,{"derivedFrom":[subQ1,subQ0]});Q146=makeQuery(id+"F0.imprint","IMPRINT",FACE,{"disambiguationData":[TD([[makeQuery(id+"F0.imprint","IMPRINT",EDGE,{"disambiguationData":[TD([[subQ2,-1.0]])],"derivedFrom":subQ1}),1.0]])]});}
            var Q147;
            {var subQ0=sQuery(id+"F0.wireOp",EDGE,"E24.MirrorCS");var subQ1=sQuery(id+"F0.wireOp",EDGE,"E10.MirrorCS");var subQ2=makeQuery(id+"F0.imprint","INTERSECT",VERTEX,{"derivedFrom":[subQ1,subQ0]});Q147=makeQuery(id+"F0.imprint","IMPRINT",FACE,{"disambiguationData":[TD([[makeQuery(id+"F0.imprint","IMPRINT",EDGE,{"disambiguationData":[TD([[subQ2,-1.0]])],"derivedFrom":subQ1}),1.0]])]});}
            var Q148;
            {var subQ0=sQuery(id+"F0.wireOp",EDGE,"E24.MirrorCS");var subQ1=sQuery(id+"F0.wireOp",EDGE,"E6.bottom");var subQ2=makeQuery(id+"F0.imprint","INTERSECT",VERTEX,{"derivedFrom":[subQ1,subQ0]});Q148=makeQuery(id+"F0.imprint","IMPRINT",FACE,{"disambiguationData":[TD([[makeQuery(id+"F0.imprint","IMPRINT",EDGE,{"disambiguationData":[TD([[subQ2,-1.0]])],"derivedFrom":subQ1}),1.0]])]});}
            var Q149;
            {var subQ0=sQuery(id+"F0.wireOp",EDGE,"E26.MirrorCS");var subQ1=sQuery(id+"F0.wireOp",EDGE,"E13.MirrorCS");var subQ2=makeQuery(id+"F0.imprint","INTERSECT",VERTEX,{"derivedFrom":[subQ1,subQ0]});Q149=makeQuery(id+"F0.imprint","IMPRINT",FACE,{"disambiguationData":[TD([[makeQuery(id+"F0.imprint","IMPRINT",EDGE,{"disambiguationData":[TD([[subQ2,-1.0]])],"derivedFrom":subQ1}),1.0]])]});}
            var Q150;
            {var subQ0=sQuery(id+"F0.wireOp",EDGE,"E26.MirrorCS");var subQ1=sQuery(id+"F0.wireOp",EDGE,"E12.MirrorCS");var subQ2=makeQuery(id+"F0.imprint","INTERSECT",VERTEX,{"derivedFrom":[subQ1,subQ0]});Q150=makeQuery(id+"F0.imprint","IMPRINT",FACE,{"disambiguationData":[TD([[makeQuery(id+"F0.imprint","IMPRINT",EDGE,{"disambiguationData":[TD([[subQ2,-1.0]])],"derivedFrom":subQ1}),1.0]])]});}
            var Q151;
            {var subQ0=sQuery(id+"F0.wireOp",EDGE,"E22.MirrorCS");var subQ1=sQuery(id+"F0.wireOp",EDGE,"E6.bottom");var subQ2=makeQuery(id+"F0.imprint","INTERSECT",VERTEX,{"derivedFrom":[subQ1,subQ0]});Q151=makeQuery(id+"F0.imprint","IMPRINT",FACE,{"disambiguationData":[TD([[makeQuery(id+"F0.imprint","IMPRINT",EDGE,{"disambiguationData":[TD([[subQ2,-1.0]])],"derivedFrom":subQ1}),1.0]])]});}
            var Q152;
            {var subQ0=sQuery(id+"F0.wireOp",EDGE,"E22.MirrorCS");var subQ1=sQuery(id+"F0.wireOp",EDGE,"E7.bottom");var subQ2=makeQuery(id+"F0.imprint","INTERSECT",VERTEX,{"derivedFrom":[subQ1,subQ0]});Q152=makeQuery(id+"F0.imprint","IMPRINT",FACE,{"disambiguationData":[TD([[makeQuery(id+"F0.imprint","IMPRINT",EDGE,{"disambiguationData":[TD([[subQ2,-1.0]])],"derivedFrom":subQ1}),-1.0]])]});}
            var Q153;
            {var subQ0=sQuery(id+"F0.wireOp",EDGE,"E19.MirrorCS");var subQ1=sQuery(id+"F0.wireOp",EDGE,"E8.bottom");var subQ2=makeQuery(id+"F0.imprint","INTERSECT",VERTEX,{"derivedFrom":[subQ1,subQ0]});Q153=makeQuery(id+"F0.imprint","IMPRINT",FACE,{"disambiguationData":[TD([[makeQuery(id+"F0.imprint","IMPRINT",EDGE,{"disambiguationData":[TD([[subQ2,-1.0]])],"derivedFrom":subQ1}),-1.0]])]});}
            var Q154;
            {var subQ0=sQuery(id+"F0.wireOp",EDGE,"E20.MirrorCS");var subQ1=sQuery(id+"F0.wireOp",EDGE,"E5");var subQ2=makeQuery(id+"F0.imprint","INTERSECT",VERTEX,{"disambiguationData":[OD(0.0)],"derivedFrom":[subQ1,subQ0]});Q154=makeQuery(id+"F0.imprint","IMPRINT",FACE,{"disambiguationData":[TD([[makeQuery(id+"F0.imprint","IMPRINT",EDGE,{"disambiguationData":[TD([[subQ2,-1.0]])],"derivedFrom":subQ1}),1.0]])]});}
            var Q155;
            {var subQ0=sQuery(id+"F0.wireOp",EDGE,"E20.MirrorCS");var subQ1=sQuery(id+"F0.wireOp",EDGE,"E8.bottom");var subQ2=makeQuery(id+"F0.imprint","INTERSECT",VERTEX,{"derivedFrom":[subQ1,subQ0]});Q155=makeQuery(id+"F0.imprint","IMPRINT",FACE,{"disambiguationData":[TD([[makeQuery(id+"F0.imprint","IMPRINT",EDGE,{"disambiguationData":[TD([[subQ2,-1.0]])],"derivedFrom":subQ1}),-1.0]])]});}
            var Q156;
            {var subQ0=sQuery(id+"F0.wireOp",EDGE,"E24.MirrorCS");var subQ1=sQuery(id+"F0.wireOp",EDGE,"E8.bottom");var subQ2=makeQuery(id+"F0.imprint","INTERSECT",VERTEX,{"derivedFrom":[subQ1,subQ0]});Q156=makeQuery(id+"F0.imprint","IMPRINT",FACE,{"disambiguationData":[TD([[makeQuery(id+"F0.imprint","IMPRINT",EDGE,{"disambiguationData":[TD([[subQ2,-1.0]])],"derivedFrom":subQ1}),-1.0]])]});}
            var Q157;
            {var subQ0=sQuery(id+"F0.wireOp",EDGE,"E24.MirrorCS");var subQ1=sQuery(id+"F0.wireOp",EDGE,"E7.bottom");var subQ2=makeQuery(id+"F0.imprint","INTERSECT",VERTEX,{"derivedFrom":[subQ1,subQ0]});Q157=makeQuery(id+"F0.imprint","IMPRINT",FACE,{"disambiguationData":[TD([[makeQuery(id+"F0.imprint","IMPRINT",EDGE,{"disambiguationData":[TD([[subQ2,-1.0]])],"derivedFrom":subQ1}),-1.0]])]});}
            var Q158;
            {var subQ0=sQuery(id+"F0.wireOp",EDGE,"E18.MirrorCS");var subQ1=sQuery(id+"F0.wireOp",EDGE,"E7.bottom");var subQ2=makeQuery(id+"F0.imprint","INTERSECT",VERTEX,{"derivedFrom":[subQ1,subQ0]});Q158=makeQuery(id+"F0.imprint","IMPRINT",FACE,{"disambiguationData":[TD([[makeQuery(id+"F0.imprint","IMPRINT",EDGE,{"disambiguationData":[TD([[subQ2,-1.0]])],"derivedFrom":subQ1}),-1.0]])]});}
            var Q159;
            {var subQ0=sQuery(id+"F0.wireOp",EDGE,"E20.MirrorCS");var subQ1=sQuery(id+"F0.wireOp",EDGE,"E7.bottom");var subQ2=makeQuery(id+"F0.imprint","INTERSECT",VERTEX,{"derivedFrom":[subQ1,subQ0]});Q159=makeQuery(id+"F0.imprint","IMPRINT",FACE,{"disambiguationData":[TD([[makeQuery(id+"F0.imprint","IMPRINT",EDGE,{"disambiguationData":[TD([[subQ2,-1.0]])],"derivedFrom":subQ1}),-1.0]])]});}
            var Q160;
            {var subQ0=sQuery(id+"F0.wireOp",EDGE,"E19.MirrorCS");var subQ1=sQuery(id+"F0.wireOp",EDGE,"E7.top");var subQ2=makeQuery(id+"F0.imprint","INTERSECT",VERTEX,{"derivedFrom":[subQ1,subQ0]});Q160=makeQuery(id+"F0.imprint","IMPRINT",FACE,{"disambiguationData":[TD([[makeQuery(id+"F0.imprint","IMPRINT",EDGE,{"disambiguationData":[TD([[subQ2,1.0]])],"derivedFrom":subQ1}),1.0]])]});}
            var Q161;
            {var subQ0=sQuery(id+"F0.wireOp",EDGE,"E20.MirrorCS");var subQ1=sQuery(id+"F0.wireOp",EDGE,"E6.top");var subQ2=makeQuery(id+"F0.imprint","INTERSECT",VERTEX,{"derivedFrom":[subQ1,subQ0]});Q161=makeQuery(id+"F0.imprint","IMPRINT",FACE,{"disambiguationData":[TD([[makeQuery(id+"F0.imprint","IMPRINT",EDGE,{"disambiguationData":[TD([[subQ2,-1.0]])],"derivedFrom":subQ1}),-1.0]])]});}
            extrude(context, id + "F1", {"entities" : qUnion([Q0, Q1, Q2, Q3, Q4, Q5, Q6, Q7, Q8, Q9, Q10, Q11, Q12, Q13, Q14, Q15, Q16, Q17, Q18, Q19, Q20, Q21, Q22, Q23, Q24, Q25, Q26, Q27, Q28, Q29, Q30, Q31, Q32, Q33, Q34, Q35, Q36, Q37, Q38, Q39, Q40, Q41, Q42, Q43, Q44, Q45, Q46, Q47, Q48, Q49, Q50, Q51, Q52, Q53, Q54, Q55, Q56, Q57, Q58, Q59, Q60, Q61, Q62, Q63, Q64, Q65, Q66, Q67, Q68, Q69, Q70, Q71, Q72, Q73, Q74, Q75, Q76, Q77, Q78, Q79, Q80, Q81, Q82, Q83, Q84, Q85, Q86, Q87, Q88, Q89, Q90, Q91, Q92, Q93, Q94, Q95, Q96, Q97, Q98, Q99, Q100, Q101, Q102, Q103, Q104, Q105, Q106, Q107, Q108, Q109, Q110, Q111, Q112, Q113, Q114, Q115, Q116, Q117, Q118, Q119, Q120, Q121, Q122, Q123, Q124, Q125, Q126, Q127, Q128, Q129, Q130, Q131, Q132, Q133, Q134, Q135, Q136, Q137, Q138, Q139, Q140, Q141, Q142, Q143, Q144, Q145, Q146, Q147, Q148, Q149, Q150, Q151, Q152, Q153, Q154, Q155, Q156, Q157, Q158, Q159, Q160, Q161]), "depth" : 1.5 * mm, "offsetDistance" : 25 * mm});
        }
        {
            var Q0;
            Q0=makeQuery(id+"F1.opExtrude","SWEPT_EDGE",EDGE,{"disambiguationData":[OSD([sQuery(id+"F0.wireOp",EDGE,"E0.top"),sQuery(id+"F0.wireOp",EDGE,"E0.right")])]});
            var Q1;
            Q1=makeQuery(id+"F1.opExtrude","SWEPT_EDGE",EDGE,{"disambiguationData":[OSD([sQuery(id+"F0.wireOp",EDGE,"E0.top"),sQuery(id+"F0.wireOp",EDGE,"E0.left")])]});
            var Q2;
            Q2=makeQuery(id+"F1.opExtrude","SWEPT_EDGE",EDGE,{"disambiguationData":[OSD([sQuery(id+"F0.wireOp",EDGE,"E0.bottom"),sQuery(id+"F0.wireOp",EDGE,"E0.left")])]});
            var Q3;
            Q3=makeQuery(id+"F1.opExtrude","SWEPT_EDGE",EDGE,{"disambiguationData":[OSD([sQuery(id+"F0.wireOp",EDGE,"E0.bottom"),sQuery(id+"F0.wireOp",EDGE,"E0.right")])]});
            fillet(context, id + "F2", {"entities" : qUnion([Q0, Q1, Q2, Q3]), "radius" : 3 * mm, "tangentPropagation" : true, "allowEdgeOverflow" : false});
        }
        {
            var Q0;
            Q0=makeQuery(id+"F1.opExtrude","CAP_FACE",FACE,{"disambiguationData":[OSD([sQuery(id+"F0.wireOp",EDGE,"E0.bottom"),sQuery(id+"F0.wireOp",EDGE,"E0.top"),sQuery(id+"F0.wireOp",EDGE,"E0.left"),sQuery(id+"F0.wireOp",EDGE,"E0.right"),sQuery(id+"F0.wireOp",EDGE,"E1"),sQuery(id+"F0.wireOp",EDGE,"E2.MirrorC"),sQuery(id+"F0.wireOp",EDGE,"E3.MirrorC"),sQuery(id+"F0.wireOp",EDGE,"E4.MirrorC"),sQuery(id+"F0.wireOp",EDGE,"E5"),sQuery(id+"F0.wireOp",EDGE,"E6.bottom"),sQuery(id+"F0.wireOp",EDGE,"E6.top"),sQuery(id+"F0.wireOp",EDGE,"E7.bottom"),sQuery(id+"F0.wireOp",EDGE,"E7.top"),sQuery(id+"F0.wireOp",EDGE,"E8.bottom"),sQuery(id+"F0.wireOp",EDGE,"E8.top"),sQuery(id+"F0.wireOp",EDGE,"E10.MirrorCS"),sQuery(id+"F0.wireOp",EDGE,"E11.MirrorCS"),sQuery(id+"F0.wireOp",EDGE,"E12.MirrorCS"),sQuery(id+"F0.wireOp",EDGE,"E13.MirrorCS"),sQuery(id+"F0.wireOp",EDGE,"E14.MirrorCS"),sQuery(id+"F0.wireOp",EDGE,"E15.MirrorCS"),sQuery(id+"F0.wireOp",EDGE,"E16.MirrorCS"),sQuery(id+"F0.wireOp",EDGE,"E17.MirrorCS"),sQuery(id+"F0.wireOp",EDGE,"E18.MirrorCS"),sQuery(id+"F0.wireOp",EDGE,"E19.MirrorCS"),sQuery(id+"F0.wireOp",EDGE,"E20.MirrorCS"),sQuery(id+"F0.wireOp",EDGE,"E21.MirrorCS"),sQuery(id+"F0.wireOp",EDGE,"E22.MirrorCS"),sQuery(id+"F0.wireOp",EDGE,"E23.MirrorCS"),sQuery(id+"F0.wireOp",EDGE,"E24.MirrorCS"),sQuery(id+"F0.wireOp",EDGE,"E25.MirrorCS"),sQuery(id+"F0.wireOp",EDGE,"E26.MirrorCS"),sQuery(id+"F0.wireOp",EDGE,"E27.MirrorCS")])],"isStart":false});
            var sketch = newSketch(context, id + "F3", { "sketchPlane" : qUnion([Q0])});
            skLineSegment(sketch, "E28.bottom", {"start": v(38.5, 38.5) * mm, "end": v(-38.5, 38.5) * mm});
            skLineSegment(sketch, "E28.top", {"start": v(38.5, -38.5) * mm, "end": v(-38.5, -38.5) * mm});
            skLineSegment(sketch, "E28.left", {"start": v(38.5, 38.5) * mm, "end": v(38.5, -38.5) * mm});
            skLineSegment(sketch, "E28.right", {"start": v(-38.5, 38.5) * mm, "end": v(-38.5, -38.5) * mm});
            skPoint(sketch, "E28.middle", {"position": v(0, 0) * mm});
            skCircle(sketch, "E29", {"center": v(-36, 36) * mm, "radius": 4 * mm});
            skCircle(sketch, "E30.MirrorC", {"center": v(36, 36) * mm, "radius": 4 * mm});
            skCircle(sketch, "E31.MirrorC", {"center": v(-36, -36) * mm, "radius": 4 * mm});
            skCircle(sketch, "E32.MirrorC", {"center": v(36, -36) * mm, "radius": 4 * mm});
            skSolve(sketch);
        }
        {
            var Q0;
            {var subQ0=sQuery(id+"F3.wireOp",EDGE,"E28.left");var subQ1=sQuery(id+"F3.wireOp",EDGE,"E28.bottom");var subQ2=makeQuery(id+"F3.imprint","INTERSECT",VERTEX,{"derivedFrom":[subQ1,subQ0]});Q0=makeQuery(id+"F3.imprint","IMPRINT",FACE,{"disambiguationData":[TD([[makeQuery(id+"F3.imprint","IMPRINT",EDGE,{"disambiguationData":[TD([[subQ2,-1.0]])],"derivedFrom":subQ1}),1.0]])]});}
            var Q1;
            {var subQ0=sQuery(id+"F3.wireOp",EDGE,"E28.left");var subQ1=sQuery(id+"F3.wireOp",EDGE,"E28.top");var subQ2=makeQuery(id+"F3.imprint","INTERSECT",VERTEX,{"derivedFrom":[subQ1,subQ0]});Q1=makeQuery(id+"F3.imprint","IMPRINT",FACE,{"disambiguationData":[TD([[makeQuery(id+"F3.imprint","IMPRINT",EDGE,{"disambiguationData":[TD([[subQ2,-1.0]])],"derivedFrom":subQ1}),-1.0]])]});}
            var Q2;
            {var subQ0=sQuery(id+"F3.wireOp",EDGE,"E28.right");var subQ1=sQuery(id+"F3.wireOp",EDGE,"E28.top");var subQ2=makeQuery(id+"F3.imprint","INTERSECT",VERTEX,{"derivedFrom":[subQ1,subQ0]});Q2=makeQuery(id+"F3.imprint","IMPRINT",FACE,{"disambiguationData":[TD([[makeQuery(id+"F3.imprint","IMPRINT",EDGE,{"disambiguationData":[TD([[subQ2,1.0]])],"derivedFrom":subQ1}),-1.0]])]});}
            var Q3;
            {var subQ22=sQuery(id+"F0.wireOp",EDGE,"E0.bottom");Q3=makeQuery(id+"F3.imprint","IMPRINT",FACE,{"disambiguationData":[TD([[makeQuery(id+"F3.imprint","IMPRINT",EDGE,{"derivedFrom":makeQuery(id+"F1.opExtrude","CAP_EDGE",EDGE,{"disambiguationData":[OSD([subQ22])],"isStart":false})}),1.0]])]});}
            var Q4;
            {var subQ0=sQuery(id+"F3.wireOp",EDGE,"E28.right");var subQ1=sQuery(id+"F3.wireOp",EDGE,"E28.bottom");var subQ2=makeQuery(id+"F3.imprint","INTERSECT",VERTEX,{"derivedFrom":[subQ1,subQ0]});Q4=makeQuery(id+"F3.imprint","IMPRINT",FACE,{"disambiguationData":[TD([[makeQuery(id+"F3.imprint","IMPRINT",EDGE,{"disambiguationData":[TD([[subQ2,1.0]])],"derivedFrom":subQ1}),1.0]])]});}
            var Q5;
            {var subQ0=sQuery(id+"F3.wireOp",EDGE,"E29");var subQ6=sQuery(id+"F3.wireOp",EDGE,"E28.bottom");var subQ9=makeQuery(id+"F3.imprint","INTERSECT",VERTEX,{"derivedFrom":[subQ6,subQ0]});Q5=makeQuery(id+"F3.imprint","IMPRINT",FACE,{"disambiguationData":[TD([[makeQuery(id+"F3.imprint","IMPRINT",EDGE,{"disambiguationData":[TD([[subQ9,-1.0]])],"derivedFrom":subQ6}),-1.0]])]});}
            var Q6;
            {var subQ0=sQuery(id+"F3.wireOp",EDGE,"E29");var subQ1=sQuery(id+"F3.wireOp",EDGE,"E28.bottom");var subQ2=makeQuery(id+"F3.imprint","INTERSECT",VERTEX,{"derivedFrom":[subQ1,subQ0]});Q6=makeQuery(id+"F3.imprint","IMPRINT",FACE,{"disambiguationData":[TD([[makeQuery(id+"F3.imprint","IMPRINT",EDGE,{"disambiguationData":[TD([[subQ2,-1.0]])],"derivedFrom":subQ1}),1.0]])]});}
            var Q7;
            {var subQ5=sQuery(id+"F0.wireOp",EDGE,"E0.right");var subQ6=makeQuery(id+"F1.opExtrude","CAP_EDGE",EDGE,{"disambiguationData":[OSD([subQ5])],"isStart":false});Q7=makeQuery(id+"F3.imprint","IMPRINT",FACE,{"disambiguationData":[TD([[makeQuery(id+"F3.imprint","IMPRINT",EDGE,{"derivedFrom":subQ6}),1.0]])]});}
            var Q8;
            {var subQ5=sQuery(id+"F0.wireOp",EDGE,"E0.left");var subQ6=makeQuery(id+"F1.opExtrude","CAP_EDGE",EDGE,{"disambiguationData":[OSD([subQ5])],"isStart":false});Q8=makeQuery(id+"F3.imprint","IMPRINT",FACE,{"disambiguationData":[TD([[makeQuery(id+"F3.imprint","IMPRINT",EDGE,{"derivedFrom":subQ6}),-1.0]])]});}
            var Q9;
            {var subQ1=sQuery(id+"F3.wireOp",EDGE,"E28.left");var subQ6=sQuery(id+"F3.wireOp",EDGE,"E28.bottom");var subQ7=makeQuery(id+"F3.imprint","INTERSECT",VERTEX,{"derivedFrom":[subQ6,subQ1]});Q9=makeQuery(id+"F3.imprint","IMPRINT",FACE,{"disambiguationData":[TD([[makeQuery(id+"F3.imprint","IMPRINT",EDGE,{"disambiguationData":[TD([[subQ7,-1.0]])],"derivedFrom":subQ6}),-1.0]])]});}
            var Q10;
            {var subQ0=sQuery(id+"F3.wireOp",EDGE,"E30.MirrorC");var subQ1=sQuery(id+"F3.wireOp",EDGE,"E28.bottom");var subQ2=makeQuery(id+"F3.imprint","INTERSECT",VERTEX,{"derivedFrom":[subQ1,subQ0]});Q10=makeQuery(id+"F3.imprint","IMPRINT",FACE,{"disambiguationData":[TD([[makeQuery(id+"F3.imprint","IMPRINT",EDGE,{"disambiguationData":[TD([[subQ2,1.0]])],"derivedFrom":subQ1}),1.0]])]});}
            var Q11;
            {var subQ0=sQuery(id+"F3.wireOp",EDGE,"E32.MirrorC");var subQ1=sQuery(id+"F3.wireOp",EDGE,"E28.top");var subQ2=makeQuery(id+"F3.imprint","INTERSECT",VERTEX,{"derivedFrom":[subQ1,subQ0]});Q11=makeQuery(id+"F3.imprint","IMPRINT",FACE,{"disambiguationData":[TD([[makeQuery(id+"F3.imprint","IMPRINT",EDGE,{"disambiguationData":[TD([[subQ2,1.0]])],"derivedFrom":subQ1}),-1.0]])]});}
            var Q12;
            {var subQ0=sQuery(id+"F3.wireOp",EDGE,"E28.left");var subQ1=sQuery(id+"F3.wireOp",EDGE,"E28.top");var subQ2=makeQuery(id+"F3.imprint","INTERSECT",VERTEX,{"derivedFrom":[subQ1,subQ0]});Q12=makeQuery(id+"F3.imprint","IMPRINT",FACE,{"disambiguationData":[TD([[makeQuery(id+"F3.imprint","IMPRINT",EDGE,{"disambiguationData":[TD([[subQ2,-1.0]])],"derivedFrom":subQ1}),1.0]])]});}
            var Q13;
            {var subQ5=sQuery(id+"F0.wireOp",EDGE,"E0.top");var subQ6=makeQuery(id+"F1.opExtrude","CAP_EDGE",EDGE,{"disambiguationData":[OSD([subQ5])],"isStart":false});Q13=makeQuery(id+"F3.imprint","IMPRINT",FACE,{"disambiguationData":[TD([[makeQuery(id+"F3.imprint","IMPRINT",EDGE,{"derivedFrom":subQ6}),-1.0]])]});}
            var Q14;
            {var subQ0=sQuery(id+"F3.wireOp",EDGE,"E31.MirrorC");var subQ1=sQuery(id+"F3.wireOp",EDGE,"E28.top");var subQ2=makeQuery(id+"F3.imprint","INTERSECT",VERTEX,{"derivedFrom":[subQ1,subQ0]});Q14=makeQuery(id+"F3.imprint","IMPRINT",FACE,{"disambiguationData":[TD([[makeQuery(id+"F3.imprint","IMPRINT",EDGE,{"disambiguationData":[TD([[subQ2,-1.0]])],"derivedFrom":subQ1}),-1.0]])]});}
            var Q15;
            {var subQ0=sQuery(id+"F3.wireOp",EDGE,"E29");var subQ1=sQuery(id+"F3.wireOp",EDGE,"E28.bottom");var subQ2=makeQuery(id+"F3.imprint","INTERSECT",VERTEX,{"disambiguationData":[OD(0.0)],"derivedFrom":[subQ1,subQ0]});Q15=makeQuery(id+"F3.imprint","IMPRINT",FACE,{"disambiguationData":[TD([[makeQuery(id+"F3.imprint","IMPRINT",EDGE,{"disambiguationData":[TD([[subQ2,-1.0]])],"derivedFrom":subQ1}),1.0]])]});}
            var Q16;
            {var subQ0=sQuery(id+"F3.wireOp",EDGE,"E29");var subQ1=sQuery(id+"F3.wireOp",EDGE,"E28.right");var subQ2=makeQuery(id+"F3.imprint","INTERSECT",VERTEX,{"disambiguationData":[OD(0.0)],"derivedFrom":[subQ1,subQ0]});Q16=makeQuery(id+"F3.imprint","IMPRINT",FACE,{"disambiguationData":[TD([[makeQuery(id+"F3.imprint","IMPRINT",EDGE,{"disambiguationData":[TD([[subQ2,-1.0]])],"derivedFrom":subQ1}),-1.0]])]});}
            var Q17;
            {var subQ0=sQuery(id+"F3.wireOp",EDGE,"E30.MirrorC");var subQ1=sQuery(id+"F3.wireOp",EDGE,"E28.bottom");var subQ2=makeQuery(id+"F3.imprint","INTERSECT",VERTEX,{"disambiguationData":[OD(1.0)],"derivedFrom":[subQ1,subQ0]});Q17=makeQuery(id+"F3.imprint","IMPRINT",FACE,{"disambiguationData":[TD([[makeQuery(id+"F3.imprint","IMPRINT",EDGE,{"disambiguationData":[TD([[subQ2,1.0]])],"derivedFrom":subQ1}),1.0]])]});}
            var Q18;
            {var subQ0=sQuery(id+"F3.wireOp",EDGE,"E30.MirrorC");var subQ1=sQuery(id+"F3.wireOp",EDGE,"E28.bottom");var subQ2=makeQuery(id+"F3.imprint","INTERSECT",VERTEX,{"disambiguationData":[OD(0.0)],"derivedFrom":[subQ1,subQ0]});Q18=makeQuery(id+"F3.imprint","IMPRINT",FACE,{"disambiguationData":[TD([[makeQuery(id+"F3.imprint","IMPRINT",EDGE,{"disambiguationData":[TD([[subQ2,-1.0]])],"derivedFrom":subQ1}),-1.0]])]});}
            var Q19;
            {var subQ0=sQuery(id+"F3.wireOp",EDGE,"E30.MirrorC");var subQ1=sQuery(id+"F3.wireOp",EDGE,"E28.left");var subQ2=makeQuery(id+"F3.imprint","INTERSECT",VERTEX,{"disambiguationData":[OD(0.0)],"derivedFrom":[subQ1,subQ0]});Q19=makeQuery(id+"F3.imprint","IMPRINT",FACE,{"disambiguationData":[TD([[makeQuery(id+"F3.imprint","IMPRINT",EDGE,{"disambiguationData":[TD([[subQ2,-1.0]])],"derivedFrom":subQ1}),1.0]])]});}
            var Q20;
            {var subQ0=sQuery(id+"F3.wireOp",EDGE,"E32.MirrorC");var subQ1=sQuery(id+"F3.wireOp",EDGE,"E28.top");var subQ2=makeQuery(id+"F3.imprint","INTERSECT",VERTEX,{"disambiguationData":[OD(0.0)],"derivedFrom":[subQ1,subQ0]});Q20=makeQuery(id+"F3.imprint","IMPRINT",FACE,{"disambiguationData":[TD([[makeQuery(id+"F3.imprint","IMPRINT",EDGE,{"disambiguationData":[TD([[subQ2,-1.0]])],"derivedFrom":subQ1}),1.0]])]});}
            var Q21;
            {var subQ0=sQuery(id+"F3.wireOp",EDGE,"E32.MirrorC");var subQ1=sQuery(id+"F3.wireOp",EDGE,"E28.left");var subQ2=makeQuery(id+"F3.imprint","INTERSECT",VERTEX,{"disambiguationData":[OD(0.0)],"derivedFrom":[subQ1,subQ0]});Q21=makeQuery(id+"F3.imprint","IMPRINT",FACE,{"disambiguationData":[TD([[makeQuery(id+"F3.imprint","IMPRINT",EDGE,{"disambiguationData":[TD([[subQ2,-1.0]])],"derivedFrom":subQ1}),1.0]])]});}
            var Q22;
            {var subQ0=sQuery(id+"F3.wireOp",EDGE,"E32.MirrorC");var subQ1=sQuery(id+"F3.wireOp",EDGE,"E28.top");var subQ2=makeQuery(id+"F3.imprint","INTERSECT",VERTEX,{"disambiguationData":[OD(1.0)],"derivedFrom":[subQ1,subQ0]});Q22=makeQuery(id+"F3.imprint","IMPRINT",FACE,{"disambiguationData":[TD([[makeQuery(id+"F3.imprint","IMPRINT",EDGE,{"disambiguationData":[TD([[subQ2,1.0]])],"derivedFrom":subQ1}),-1.0]])]});}
            var Q23;
            {var subQ0=sQuery(id+"F3.wireOp",EDGE,"E31.MirrorC");var subQ1=sQuery(id+"F3.wireOp",EDGE,"E28.top");var subQ2=makeQuery(id+"F3.imprint","INTERSECT",VERTEX,{"disambiguationData":[OD(0.0)],"derivedFrom":[subQ1,subQ0]});Q23=makeQuery(id+"F3.imprint","IMPRINT",FACE,{"disambiguationData":[TD([[makeQuery(id+"F3.imprint","IMPRINT",EDGE,{"disambiguationData":[TD([[subQ2,-1.0]])],"derivedFrom":subQ1}),-1.0]])]});}
            var Q24;
            {var subQ0=sQuery(id+"F3.wireOp",EDGE,"E31.MirrorC");var subQ1=sQuery(id+"F3.wireOp",EDGE,"E28.right");var subQ2=makeQuery(id+"F3.imprint","INTERSECT",VERTEX,{"disambiguationData":[OD(0.0)],"derivedFrom":[subQ1,subQ0]});Q24=makeQuery(id+"F3.imprint","IMPRINT",FACE,{"disambiguationData":[TD([[makeQuery(id+"F3.imprint","IMPRINT",EDGE,{"disambiguationData":[TD([[subQ2,-1.0]])],"derivedFrom":subQ1}),-1.0]])]});}
            var Q25;
            {var subQ0=sQuery(id+"F3.wireOp",EDGE,"E31.MirrorC");var subQ1=sQuery(id+"F3.wireOp",EDGE,"E28.top");var subQ2=makeQuery(id+"F3.imprint","INTERSECT",VERTEX,{"disambiguationData":[OD(0.0)],"derivedFrom":[subQ1,subQ0]});Q25=makeQuery(id+"F3.imprint","IMPRINT",FACE,{"disambiguationData":[TD([[makeQuery(id+"F3.imprint","IMPRINT",EDGE,{"disambiguationData":[TD([[subQ2,-1.0]])],"derivedFrom":subQ1}),1.0]])]});}
            extrude(context, id + "F4", {"entities" : qUnion([Q0, Q1, Q2, Q3, Q4, Q5, Q6, Q7, Q8, Q9, Q10, Q11, Q12, Q13, Q14, Q15, Q16, Q17, Q18, Q19, Q20, Q21, Q22, Q23, Q24, Q25]), "operationType" : NewBodyOperationType.ADD, "depth" : 4.5 * mm, "offsetDistance" : 25 * mm});
        }
        {
            var Q0;
            Q0=makeQuery(id+"F4.opExtrude","CAP_FACE",FACE,{"disambiguationData":[OSD([sQuery(id+"F0.wireOp",EDGE,"E0.bottom"),sQuery(id+"F0.wireOp",EDGE,"E0.top"),sQuery(id+"F0.wireOp",EDGE,"E0.left"),sQuery(id+"F0.wireOp",EDGE,"E0.right"),sQuery(id+"F0.wireOp",EDGE,"E1"),sQuery(id+"F0.wireOp",EDGE,"E2.MirrorC"),sQuery(id+"F0.wireOp",EDGE,"E3.MirrorC"),sQuery(id+"F0.wireOp",EDGE,"E4.MirrorC"),sQuery(id+"F0.wireOp",EDGE,"E5"),sQuery(id+"F0.wireOp",EDGE,"E6.bottom"),sQuery(id+"F0.wireOp",EDGE,"E6.top"),sQuery(id+"F0.wireOp",EDGE,"E7.bottom"),sQuery(id+"F0.wireOp",EDGE,"E7.top"),sQuery(id+"F0.wireOp",EDGE,"E8.bottom"),sQuery(id+"F0.wireOp",EDGE,"E8.top"),sQuery(id+"F0.wireOp",EDGE,"E9"),sQuery(id+"F0.wireOp",EDGE,"E10.MirrorCS"),sQuery(id+"F0.wireOp",EDGE,"E11.MirrorCS"),sQuery(id+"F0.wireOp",EDGE,"E12.MirrorCS"),sQuery(id+"F0.wireOp",EDGE,"E13.MirrorCS"),sQuery(id+"F0.wireOp",EDGE,"E14.MirrorCS"),sQuery(id+"F0.wireOp",EDGE,"E15.MirrorCS"),sQuery(id+"F0.wireOp",EDGE,"E16.MirrorCS"),sQuery(id+"F0.wireOp",EDGE,"E17.MirrorCS"),sQuery(id+"F0.wireOp",EDGE,"E18.MirrorCS"),sQuery(id+"F0.wireOp",EDGE,"E19.MirrorCS"),sQuery(id+"F0.wireOp",EDGE,"E20.MirrorCS"),sQuery(id+"F0.wireOp",EDGE,"E21.MirrorCS"),sQuery(id+"F0.wireOp",EDGE,"E22.MirrorCS"),sQuery(id+"F0.wireOp",EDGE,"E23.MirrorCS"),sQuery(id+"F0.wireOp",EDGE,"E24.MirrorCS"),sQuery(id+"F0.wireOp",EDGE,"E25.MirrorCS"),sQuery(id+"F0.wireOp",EDGE,"E26.MirrorCS"),sQuery(id+"F0.wireOp",EDGE,"E27.MirrorCS"),sQuery(id+"F3.wireOp",EDGE,"E28.bottom"),sQuery(id+"F3.wireOp",EDGE,"E28.top"),sQuery(id+"F3.wireOp",EDGE,"E28.left"),sQuery(id+"F3.wireOp",EDGE,"E28.right"),sQuery(id+"F3.wireOp",EDGE,"E29"),sQuery(id+"F3.wireOp",EDGE,"E30.MirrorC"),sQuery(id+"F3.wireOp",EDGE,"E31.MirrorC"),sQuery(id+"F3.wireOp",EDGE,"E32.MirrorC")])],"isStart":false});
            var sketch = newSketch(context, id + "F5", { "sketchPlane" : qUnion([Q0])});
            skLineSegment(sketch, "E33.bottom", {"start": v(-10, 38.5) * mm, "end": v(10, 38.5) * mm});
            skLineSegment(sketch, "E33.top", {"start": v(-10, 39) * mm, "end": v(10, 39) * mm});
            skLineSegment(sketch, "E33.left", {"start": v(-10, 38.5) * mm, "end": v(-10, 39) * mm});
            skLineSegment(sketch, "E33.right", {"start": v(10, 38.5) * mm, "end": v(10, 39) * mm});
            skPoint(sketch, "E33.middle", {"position": v(0, 38.75) * mm});
            skLineSegment(sketch, "E34.MirrorCS", {"start": v(-10, -38.5) * mm, "end": v(-10, -39) * mm});
            skLineSegment(sketch, "E35.MirrorCS", {"start": v(-10, -39) * mm, "end": v(10, -39) * mm});
            skLineSegment(sketch, "E36.MirrorCS", {"start": v(-10, -38.5) * mm, "end": v(10, -38.5) * mm});
            skLineSegment(sketch, "E37.MirrorCS", {"start": v(10, -38.5) * mm, "end": v(10, -39) * mm});
            skSolve(sketch);
        }
        {
            var Q0;
            Q0=makeQuery(id+"F5.imprint","IMPRINT",FACE,{"disambiguationData":[TD([[makeQuery(id+"F5.imprint","IMPRINT",EDGE,{"derivedFrom":sQuery(id+"F5.wireOp",EDGE,"E33.bottom")}),-1.0]])]});
            var Q1;
            Q1=makeQuery(id+"F5.imprint","IMPRINT",FACE,{"disambiguationData":[TD([[makeQuery(id+"F5.imprint","IMPRINT",EDGE,{"derivedFrom":sQuery(id+"F5.wireOp",EDGE,"E34.MirrorCS")}),1.0]])]});
            extrude(context, id + "F6", {"entities" : qUnion([Q0, Q1]), "operationType" : NewBodyOperationType.ADD, "depth" : 2.5 * mm, "offsetDistance" : 25 * mm});
        }
        {
            var Q0;
            Q0=makeQuery(id+"F4.opExtrude","CAP_FACE",FACE,{"disambiguationData":[OSD([sQuery(id+"F0.wireOp",EDGE,"E0.bottom"),sQuery(id+"F0.wireOp",EDGE,"E0.top"),sQuery(id+"F0.wireOp",EDGE,"E0.left"),sQuery(id+"F0.wireOp",EDGE,"E0.right"),sQuery(id+"F0.wireOp",EDGE,"E1"),sQuery(id+"F0.wireOp",EDGE,"E2.MirrorC"),sQuery(id+"F0.wireOp",EDGE,"E3.MirrorC"),sQuery(id+"F0.wireOp",EDGE,"E4.MirrorC"),sQuery(id+"F0.wireOp",EDGE,"E5"),sQuery(id+"F0.wireOp",EDGE,"E6.bottom"),sQuery(id+"F0.wireOp",EDGE,"E6.top"),sQuery(id+"F0.wireOp",EDGE,"E7.bottom"),sQuery(id+"F0.wireOp",EDGE,"E7.top"),sQuery(id+"F0.wireOp",EDGE,"E8.bottom"),sQuery(id+"F0.wireOp",EDGE,"E8.top"),sQuery(id+"F0.wireOp",EDGE,"E9"),sQuery(id+"F0.wireOp",EDGE,"E10.MirrorCS"),sQuery(id+"F0.wireOp",EDGE,"E11.MirrorCS"),sQuery(id+"F0.wireOp",EDGE,"E12.MirrorCS"),sQuery(id+"F0.wireOp",EDGE,"E13.MirrorCS"),sQuery(id+"F0.wireOp",EDGE,"E14.MirrorCS"),sQuery(id+"F0.wireOp",EDGE,"E15.MirrorCS"),sQuery(id+"F0.wireOp",EDGE,"E16.MirrorCS"),sQuery(id+"F0.wireOp",EDGE,"E17.MirrorCS"),sQuery(id+"F0.wireOp",EDGE,"E18.MirrorCS"),sQuery(id+"F0.wireOp",EDGE,"E19.MirrorCS"),sQuery(id+"F0.wireOp",EDGE,"E20.MirrorCS"),sQuery(id+"F0.wireOp",EDGE,"E21.MirrorCS"),sQuery(id+"F0.wireOp",EDGE,"E22.MirrorCS"),sQuery(id+"F0.wireOp",EDGE,"E23.MirrorCS"),sQuery(id+"F0.wireOp",EDGE,"E24.MirrorCS"),sQuery(id+"F0.wireOp",EDGE,"E25.MirrorCS"),sQuery(id+"F0.wireOp",EDGE,"E26.MirrorCS"),sQuery(id+"F0.wireOp",EDGE,"E27.MirrorCS"),sQuery(id+"F3.wireOp",EDGE,"E28.bottom"),sQuery(id+"F3.wireOp",EDGE,"E28.top"),sQuery(id+"F3.wireOp",EDGE,"E28.left"),sQuery(id+"F3.wireOp",EDGE,"E28.right"),sQuery(id+"F3.wireOp",EDGE,"E29"),sQuery(id+"F3.wireOp",EDGE,"E30.MirrorC"),sQuery(id+"F3.wireOp",EDGE,"E31.MirrorC"),sQuery(id+"F3.wireOp",EDGE,"E32.MirrorC")])],"isStart":false});
            var sketch = newSketch(context, id + "F7", { "sketchPlane" : qUnion([Q0])});
            skLineSegment(sketch, "E38.bottom", {"start": v(38.5, 10.1) * mm, "end": v(39.1, 10.1) * mm});
            skLineSegment(sketch, "E38.top", {"start": v(38.5, -10.1) * mm, "end": v(39.1, -10.1) * mm});
            skLineSegment(sketch, "E38.left", {"start": v(38.5, 10.1) * mm, "end": v(38.5, -10.1) * mm});
            skLineSegment(sketch, "E38.right", {"start": v(39.1, 10.1) * mm, "end": v(39.1, -10.1) * mm});
            skPoint(sketch, "E38.middle", {"position": v(38.8, 0) * mm});
            skPoint(sketch, "E38.middle.positionSnap0", {"position": v(38.5, 0) * mm});
            skPoint(sketch, "E38.centerSnap0", {"position": v(38.5, 0) * mm});
            skLineSegment(sketch, "E39.MirrorCS", {"start": v(-39.1, 10.1) * mm, "end": v(-39.1, -10.1) * mm});
            skLineSegment(sketch, "E40.MirrorCS", {"start": v(-38.5, 10.1) * mm, "end": v(-39.1, 10.1) * mm});
            skLineSegment(sketch, "E41.MirrorCS", {"start": v(-38.5, 10.1) * mm, "end": v(-38.5, -10.1) * mm});
            skLineSegment(sketch, "E42.MirrorCS", {"start": v(-38.5, -10.1) * mm, "end": v(-39.1, -10.1) * mm});
            skSolve(sketch);
        }
        {
            var Q0;
            Q0=makeQuery(id+"F7.imprint","IMPRINT",FACE,{"disambiguationData":[TD([[makeQuery(id+"F7.imprint","IMPRINT",EDGE,{"derivedFrom":sQuery(id+"F7.wireOp",EDGE,"E39.MirrorCS")}),1.0]])]});
            var Q1;
            Q1=makeQuery(id+"F7.imprint","IMPRINT",FACE,{"disambiguationData":[TD([[makeQuery(id+"F7.imprint","IMPRINT",EDGE,{"derivedFrom":sQuery(id+"F7.wireOp",EDGE,"E38.bottom")}),-1.0]])]});
            extrude(context, id + "F8", {"entities" : qUnion([Q0, Q1]), "operationType" : NewBodyOperationType.REMOVE, "oppositeDirection" : true, "depth" : 3 * mm, "offsetDistance" : 25 * mm});
        }
    });
